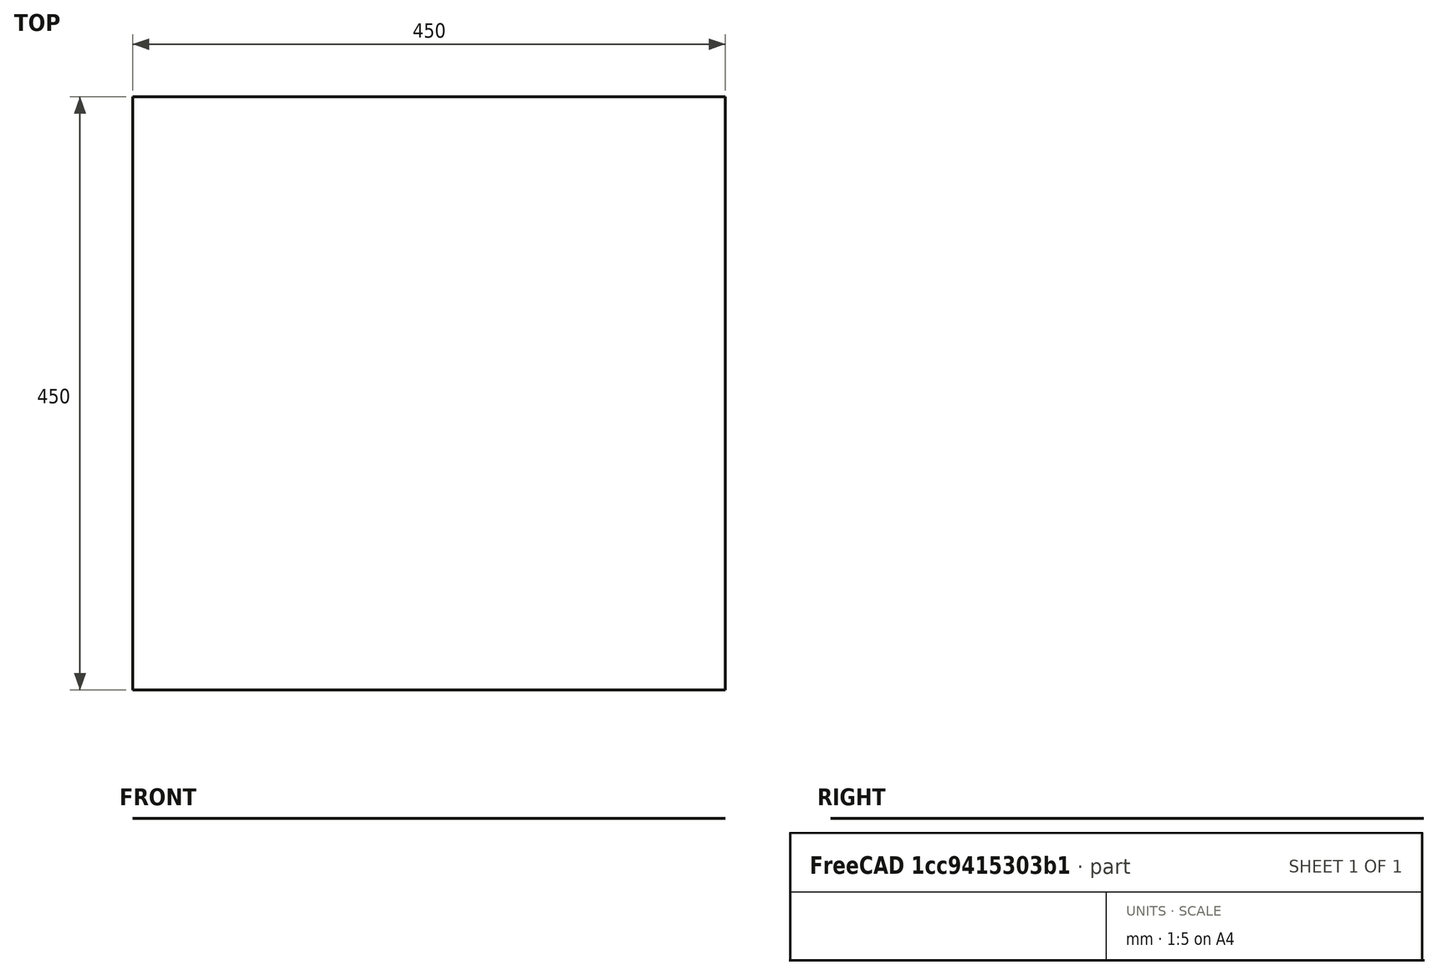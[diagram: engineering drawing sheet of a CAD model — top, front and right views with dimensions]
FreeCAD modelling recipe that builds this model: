
FCSTD DOCUMENT  (FreeCAD 0.19R18044 (Git))
Label: lift-upper-stage
License: Public Domain
LicenseURL: http://en.wikipedia.org/wiki/Public_domain
objects: App::FeaturePython×40, Part::FeaturePython×29, App::Link×6, App::LinkElement×4
note: 28 computed .brp shape members not serialized (recipe doc carries the construction recipe); baked Part::Feature solids carry a one-line shape summary decoded from their .brp
EXTERNAL_REF file=../parts/lift/upper-stage-actuator-rod.FCStd obj=Assembly
EXTERNAL_REF file=../parts/lift/upper-stage-beam.FCStd obj=Assembly
EXTERNAL_REF file=../parts/lift/upper-stage-beam.FCStd obj=Assembly001
EXTERNAL_REF file=../parts/lift/upper-stage-rod.FCStd obj=Assembly
EXTERNAL_REF file=../parts/common/linear-actuator-400.FCStd obj=Assembly004
EXTERNAL_REF file=../parts/common/rail-450.FCStd obj=Assembly002

FEATURE [App::Link] Link  label="upper-stage-actuator-rod"
  LinkPlacement = pos=(9.94618e-10,3.77807,437.103) rot=(-1,0,0;4.45001rad)
  LinkedObject = -> <external ../parts/lift/upper-stage-actuator-rod.FCStd>#Assembly
  Placement = pos=(9.94618e-10,3.77807,437.103) rot=(-1,0,0;4.45001rad)
FEATURE [App::Link] Link001  label="upper-stage-beam-left"
  LinkPlacement = pos=(-128,6.52807,7.10273) rot=(0,0,1;0rad)
  LinkedObject = -> <external ../parts/lift/upper-stage-beam.FCStd>#Assembly
  Placement = pos=(-128,6.52807,7.10273) rot=(0,0,1;0rad)
FEATURE [App::Link] Link002  label="upper-stage-beam-right"
  LinkPlacement = pos=(-118,6.52807,7.10273) rot=(0,0,1;0rad)
  LinkedObject = -> <external ../parts/lift/upper-stage-beam.FCStd>#Assembly001
  Placement = pos=(-118,6.52807,7.10273) rot=(0,0,1;0rad)
FEATURE [App::Link] Link004  label="actuator_a"
  LinkPlacement = pos=(9.25419e-08,3.77807,-78.8973) rot=(0,0,1;0rad)
  LinkedObject = -> <external ../parts/common/linear-actuator-400.FCStd>#Assembly004
  Placement = pos=(9.25419e-08,3.77807,-78.8973) rot=(0,0,1;0rad)
FEATURE [App::LinkElement] Link003_i0  label="top"
  LinkPlacement = pos=(3.02068e-10,-20.4719,357.103) rot=(0,0,1;0rad)
  LinkedObject = -> <external ../parts/lift/upper-stage-rod.FCStd>#Assembly
  Placement = pos=(3.02068e-10,-20.4719,357.103) rot=(0,0,1;0rad)
FEATURE [App::LinkElement] Link003_i1  label="bottom"
  LinkPlacement = pos=(7.62902e-11,-20.4719,227.103) rot=(0,0,1;0rad)
  LinkedObject = -> <external ../parts/lift/upper-stage-rod.FCStd>#Assembly
  Placement = pos=(7.62902e-11,-20.4719,227.103) rot=(0,0,1;0rad)
FEATURE [App::Link] Link003  label="upper-stage-rod"
  ElementCount = 2
  ElementList = -> [Link003_i0,Link003_i1]
  LinkedObject = -> <external ../parts/lift/upper-stage-rod.FCStd>#Assembly
FEATURE [App::LinkElement] Link005_i0  label="rail left"
  LinkPlacement = pos=(-93.3,31.0281,457.103) rot=(0.57735,-0.57735,-0.57735;2.0944rad)
  LinkedObject = -> <external ../parts/common/rail-450.FCStd>#Assembly002
  Placement = pos=(-93.3,31.0281,457.103) rot=(0.57735,-0.57735,-0.57735;2.0944rad)
FEATURE [App::LinkElement] Link005_i1  label="rail right"
  LinkPlacement = pos=(93.3,31.0281,457.103) rot=(0.57735,0.57735,0.57735;2.0944rad)
  LinkedObject = -> <external ../parts/common/rail-450.FCStd>#Assembly002
  Placement = pos=(93.3,31.0281,457.103) rot=(0.57735,0.57735,0.57735;2.0944rad)
FEATURE [App::Link] Link005  label="rail top"
  ElementCount = 2
  ElementList = -> [Link005_i0,Link005_i1]
  LinkedObject = -> <external ../parts/common/rail-450.FCStd>#Assembly002
FEATURE [Part::FeaturePython] Parts  # WARN: FeaturePython — macro-defined, semantics opaque (R4)
  Group = -> [Link,Link001,Link002,Link003,Link004,Origin,Link005]
  GroupMode = 0
FEATURE [Part::FeaturePython] Assembly  label="lift-upper-stage"  # WARN: FeaturePython — macro-defined, semantics opaque (R4)
  AutoRelax = true
  BuildShape = 0
  Freeze = false
  Group = -> [Constraints,Elements,Parts]
  GroupMode = 1
  SolverType = 1
  Verbose = false
  _SolverType = 1
  _Version = 1
FEATURE [App::FeaturePython] Constraints  # WARN: FeaturePython — macro-defined, semantics opaque (R4)
  Group = -> [Constraint,Constraint001,Constraint002,Constraint003,Constraint004,Constraint005,Constraint006,Constraint007,Constraint008,Constraint009,Constraint010,Constraint011,Constraint012]
  GroupMode = 1
  _Version = 1
FEATURE [App::FeaturePython] Elements  # WARN: FeaturePython — macro-defined, semantics opaque (R4)
  Group = -> [_Element,_Element001,_Element002,_Element003,_Element004,_Element005,_Element006,_Element007,_Element008,_Element009,_Element010,_Element011,_Element012,_Element013,_Element015,_Element016,_Element017,_Element018,_Element019,_Element020,_Element021,_Element022,_Element023,_Element024,_Element025,Element,Element001]
  GroupMode = 1
FEATURE [App::FeaturePython] Constraint  label="Locked"  # WARN: FeaturePython — macro-defined, semantics opaque (R4)
  ConstraintType = 0
  Disabled = false
  Group = -> [ElementLink]
  GroupMode = 1
  _ConstraintType = 0
  _Parent = -> Constraints
FEATURE [App::FeaturePython] ElementLink  label="_Element"  # link proxy (typed FeaturePython)
  LinkTransform = true
  LinkedObject = -> _Element
  _Parent = -> Constraint
FEATURE [Part::FeaturePython] _Element  # link proxy (typed FeaturePython)
  Detach = false
  LinkTransform = true
  LinkedObject = -> Link [1.$Element003.]
  _Parent = -> Elements
FEATURE [Part::FeaturePython] _Element001  # link proxy (typed FeaturePython)
  Detach = false
  LinkTransform = true
  LinkedObject = -> Link [1.$left.]
  _Parent = -> Elements
FEATURE [Part::FeaturePython] _Element002  # link proxy (typed FeaturePython)
  Detach = false
  LinkTransform = true
  LinkedObject = -> Link001 [1.$actuator_rod_hole.]
  _Parent = -> Elements
FEATURE [App::FeaturePython] Constraint001  label="PlaneCoincident"  # WARN: FeaturePython — macro-defined, semantics opaque (R4)
  Angle = 0
  AnglePitch = 0
  AngleRoll = 0
  Cascade = false
  ConstraintType = 2
  Disabled = false
  Group = -> [ElementLink001,ElementLink002]
  GroupMode = 1
  LockAngle = false
  Multiply = false
  Offset = -44
  OffsetX = 0
  OffsetY = 0
  _ConstraintType = 35
  _Parent = -> Constraints
FEATURE [App::FeaturePython] ElementLink001  label="_Element001"  # link proxy (typed FeaturePython)
  LinkTransform = true
  LinkedObject = -> _Element001
  _Parent = -> Constraint001
FEATURE [App::FeaturePython] ElementLink002  label="_Element002"  # link proxy (typed FeaturePython)
  LinkTransform = true
  LinkedObject = -> _Element002
  _Parent = -> Constraint001
FEATURE [App::FeaturePython] Constraint002  label="PlaneCoincident001"  # WARN: FeaturePython — macro-defined, semantics opaque (R4)
  Angle = 0
  AnglePitch = 0
  AngleRoll = 0
  Cascade = false
  ConstraintType = 2
  Disabled = false
  Group = -> [ElementLink003,ElementLink004]
  GroupMode = 1
  LockAngle = false
  Multiply = false
  Offset = -44
  OffsetX = 0
  OffsetY = 0
  _ConstraintType = 35
  _Parent = -> Constraints
FEATURE [App::FeaturePython] ElementLink003  label="_Element003"  # link proxy (typed FeaturePython)
  LinkTransform = true
  LinkedObject = -> _Element003
  _Parent = -> Constraint002
FEATURE [Part::FeaturePython] _Element003  # link proxy (typed FeaturePython)
  Detach = false
  LinkTransform = true
  LinkedObject = -> Link002 [1.$actuator_rod_hole.]
  _Parent = -> Elements
FEATURE [App::FeaturePython] ElementLink004  label="_Element004"  # link proxy (typed FeaturePython)
  LinkTransform = true
  LinkedObject = -> _Element004
  _Parent = -> Constraint002
FEATURE [Part::FeaturePython] _Element004  # link proxy (typed FeaturePython)
  Detach = false
  LinkTransform = true
  LinkedObject = -> Link [1.$right.]
  _Parent = -> Elements
FEATURE [App::FeaturePython] Constraint003  label="AxialAlignment"  # WARN: FeaturePython — macro-defined, semantics opaque (R4)
  Angle = 0
  AnglePitch = 0
  AngleRoll = 0
  ConstraintType = 4
  Disabled = false
  Group = -> [ElementLink005,ElementLink006]
  GroupMode = 1
  LockAngle = false
  Multiply = false
  _ConstraintType = 36
  _Parent = -> Constraints
FEATURE [App::FeaturePython] ElementLink005  label="_Element005"  # link proxy (typed FeaturePython)
  LinkTransform = true
  LinkedObject = -> _Element005
  _Parent = -> Constraint003
FEATURE [Part::FeaturePython] _Element005  # link proxy (typed FeaturePython)
  Detach = false
  LinkTransform = true
  LinkedObject = -> Link [1.$middle.]
  _Parent = -> Elements
FEATURE [App::FeaturePython] ElementLink006  label="_Element006"  # link proxy (typed FeaturePython)
  LinkTransform = true
  LinkedObject = -> _Element006
  _Parent = -> Constraint003
FEATURE [Part::FeaturePython] _Element006  # link proxy (typed FeaturePython)
  Detach = false
  LinkTransform = true
  LinkedObject = -> Link004 [1.$mount_top.]
  _Parent = -> Elements
FEATURE [App::FeaturePython] Constraint004  label="PlaneCoincident002"  # WARN: FeaturePython — macro-defined, semantics opaque (R4)
  Angle = 0
  AnglePitch = 0
  AngleRoll = 0
  Cascade = false
  ConstraintType = 2
  Disabled = false
  Group = -> [ElementLink007,ElementLink008]
  GroupMode = 1
  LockAngle = false
  Multiply = false
  Offset = -119
  OffsetX = 0
  OffsetY = 0
  _ConstraintType = 35
  _Parent = -> Constraints
FEATURE [App::FeaturePython] ElementLink007  label="_Element007"  # link proxy (typed FeaturePython)
  LinkTransform = true
  LinkedObject = -> _Element007
  _Parent = -> Constraint004
FEATURE [Part::FeaturePython] _Element007  # link proxy (typed FeaturePython)
  Detach = false
  LinkTransform = true
  LinkedObject = -> Link003 [Link003_i0.1.$left.]
  _Parent = -> Elements
FEATURE [App::FeaturePython] ElementLink008  label="_Element008"  # link proxy (typed FeaturePython)
  LinkTransform = true
  LinkedObject = -> _Element008
  _Parent = -> Constraint004
FEATURE [Part::FeaturePython] _Element008  # link proxy (typed FeaturePython)
  Detach = false
  LinkTransform = true
  LinkedObject = -> Link001 [1.$tv_rod_hole_top.]
  _Parent = -> Elements
FEATURE [App::FeaturePython] Constraint005  label="PlaneCoincident003"  # WARN: FeaturePython — macro-defined, semantics opaque (R4)
  Angle = 0
  AnglePitch = 0
  AngleRoll = 0
  Cascade = false
  ConstraintType = 2
  Disabled = false
  Group = -> [ElementLink009,ElementLink010]
  GroupMode = 1
  LockAngle = false
  Multiply = false
  Offset = 119
  OffsetX = 0
  OffsetY = 0
  _ConstraintType = 35
  _Parent = -> Constraints
FEATURE [App::FeaturePython] ElementLink009  label="_Element009"  # link proxy (typed FeaturePython)
  LinkTransform = true
  LinkedObject = -> _Element009
  _Parent = -> Constraint005
FEATURE [Part::FeaturePython] _Element009  # link proxy (typed FeaturePython)
  Detach = false
  LinkTransform = true
  LinkedObject = -> Link001 [1.$tv_rod_hole_bottom.]
  _Parent = -> Elements
FEATURE [App::FeaturePython] ElementLink010  label="_Element010"  # link proxy (typed FeaturePython)
  LinkTransform = true
  LinkedObject = -> _Element010
  _Parent = -> Constraint005
FEATURE [Part::FeaturePython] _Element010  # link proxy (typed FeaturePython)
  Detach = false
  LinkTransform = true
  LinkedObject = -> Link003 [Link003_i1.1.$left.]
  _Parent = -> Elements
FEATURE [Part::FeaturePython] _Element011  # link proxy (typed FeaturePython)
  Detach = false
  LinkTransform = true
  LinkedObject = -> Link002 [1.$tv_rod_hole_top.]
  _Parent = -> Elements
FEATURE [Part::FeaturePython] _Element012  # link proxy (typed FeaturePython)
  Detach = false
  LinkTransform = true
  LinkedObject = -> Link003 [Link003_i0.1.$right.]
  _Parent = -> Elements
FEATURE [App::FeaturePython] Constraint006  label="AxialAlignment001"  # WARN: FeaturePython — macro-defined, semantics opaque (R4)
  Angle = 0
  AnglePitch = 0
  AngleRoll = 0
  ConstraintType = 4
  Disabled = false
  Group = -> [ElementLink011,ElementLink012]
  GroupMode = 1
  LockAngle = false
  Multiply = false
  _ConstraintType = 36
  _Parent = -> Constraints
FEATURE [App::FeaturePython] ElementLink011  label="_Element011"  # link proxy (typed FeaturePython)
  LinkTransform = true
  LinkedObject = -> _Element011
  _Parent = -> Constraint006
FEATURE [App::FeaturePython] ElementLink012  label="_Element012"  # link proxy (typed FeaturePython)
  LinkTransform = true
  LinkedObject = -> _Element012
  _Parent = -> Constraint006
FEATURE [Part::FeaturePython] _Element013  # link proxy (typed FeaturePython)
  Detach = false
  LinkTransform = true
  LinkedObject = -> Link001 [1.$base_edge.]
  _Parent = -> Elements
FEATURE [Part::FeaturePython] _Element015  # link proxy (typed FeaturePython)
  Detach = false
  LinkTransform = true
  LinkedObject = -> Origin [Y_Axis.]
  _Parent = -> Elements
FEATURE [App::FeaturePython] Constraint007  label="MultiParallel"  # WARN: FeaturePython — macro-defined, semantics opaque (R4)
  Angle = 0
  AnglePitch = 0
  AngleRoll = 0
  ConstraintType = 6
  Disabled = false
  Group = -> [ElementLink013,ElementLink014]
  GroupMode = 1
  LockAngle = false
  _ConstraintType = 291
  _Parent = -> Constraints
FEATURE [App::FeaturePython] ElementLink013  label="_Element015"  # link proxy (typed FeaturePython)
  LinkTransform = true
  LinkedObject = -> _Element015
  _Parent = -> Constraint007
FEATURE [App::FeaturePython] ElementLink014  label="_Element013"  # link proxy (typed FeaturePython)
  LinkTransform = true
  LinkedObject = -> _Element013
  _Parent = -> Constraint007
FEATURE [Part::FeaturePython] _Element016  # link proxy (typed FeaturePython)
  Detach = false
  LinkTransform = true
  LinkedObject = -> Link001 [1.$rail_hole_top.]
  _Parent = -> Elements
FEATURE [Part::FeaturePython] _Element017  # link proxy (typed FeaturePython)
  Detach = false
  LinkTransform = true
  LinkedObject = -> Link005 [Link005_i0.1.$mount_top.]
  _Parent = -> Elements
FEATURE [Part::FeaturePython] _Element018  # link proxy (typed FeaturePython)
  Detach = false
  LinkTransform = true
  LinkedObject = -> Link001 [1.$rail-hole-middle.]
  _Parent = -> Elements
FEATURE [Part::FeaturePython] _Element019  # link proxy (typed FeaturePython)
  Detach = false
  LinkTransform = true
  LinkedObject = -> Link005 [Link005_i0.1.$mount_middle.]
  _Parent = -> Elements
FEATURE [App::FeaturePython] Constraint008  label="PlaneCoincident004"  # WARN: FeaturePython — macro-defined, semantics opaque (R4)
  Angle = 0
  AnglePitch = 0
  AngleRoll = 0
  Cascade = false
  ConstraintType = 2
  Disabled = false
  Group = -> [ElementLink015,ElementLink016]
  GroupMode = 1
  LockAngle = false
  Multiply = false
  OffsetX = 0
  OffsetY = 0
  _ConstraintType = 35
  _Parent = -> Constraints
FEATURE [App::FeaturePython] ElementLink015  label="_Element016"  # link proxy (typed FeaturePython)
  LinkTransform = true
  LinkedObject = -> _Element016
  _Parent = -> Constraint008
FEATURE [App::FeaturePython] ElementLink016  label="_Element017"  # link proxy (typed FeaturePython)
  LinkTransform = true
  LinkedObject = -> _Element017
  _Parent = -> Constraint008
FEATURE [App::FeaturePython] Constraint009  label="PlaneCoincident005"  # WARN: FeaturePython — macro-defined, semantics opaque (R4)
  Angle = 0
  AnglePitch = 0
  AngleRoll = 0
  Cascade = false
  ConstraintType = 2
  Disabled = false
  Group = -> [ElementLink017,ElementLink018]
  GroupMode = 1
  LockAngle = false
  Multiply = false
  OffsetX = 0
  OffsetY = 0
  _ConstraintType = 35
  _Parent = -> Constraints
FEATURE [App::FeaturePython] ElementLink017  label="_Element019"  # link proxy (typed FeaturePython)
  LinkTransform = true
  LinkedObject = -> _Element019
  _Parent = -> Constraint009
FEATURE [App::FeaturePython] ElementLink018  label="_Element018"  # link proxy (typed FeaturePython)
  LinkTransform = true
  LinkedObject = -> _Element018
  _Parent = -> Constraint009
FEATURE [App::FeaturePython] Constraint010  label="PlaneCoincident006"  # WARN: FeaturePython — macro-defined, semantics opaque (R4)
  Angle = 0
  AnglePitch = 0
  AngleRoll = 0
  Cascade = false
  ConstraintType = 2
  Disabled = false
  Group = -> [ElementLink019,ElementLink020]
  GroupMode = 1
  LockAngle = false
  Multiply = false
  OffsetX = 0
  OffsetY = 0
  _ConstraintType = 35
  _Parent = -> Constraints
FEATURE [App::FeaturePython] ElementLink019  label="_Element020"  # link proxy (typed FeaturePython)
  LinkTransform = true
  LinkedObject = -> _Element020
  _Parent = -> Constraint010
FEATURE [Part::FeaturePython] _Element020  # link proxy (typed FeaturePython)
  Detach = false
  LinkTransform = true
  LinkedObject = -> Link005 [Link005_i1.1.$mount_top.]
  _Parent = -> Elements
FEATURE [App::FeaturePython] ElementLink020  label="_Element021"  # link proxy (typed FeaturePython)
  LinkTransform = true
  LinkedObject = -> _Element021
  _Parent = -> Constraint010
FEATURE [Part::FeaturePython] _Element021  # link proxy (typed FeaturePython)
  Detach = false
  LinkTransform = true
  LinkedObject = -> Link002 [1.$rail_hole_top.]
  _Parent = -> Elements
FEATURE [App::FeaturePython] Constraint011  label="PlaneCoincident007"  # WARN: FeaturePython — macro-defined, semantics opaque (R4)
  Angle = 0
  AnglePitch = 0
  AngleRoll = 0
  Cascade = false
  ConstraintType = 2
  Disabled = false
  Group = -> [ElementLink021,ElementLink022]
  GroupMode = 1
  LockAngle = false
  Multiply = false
  OffsetX = 0
  OffsetY = 0
  _ConstraintType = 35
  _Parent = -> Constraints
FEATURE [App::FeaturePython] ElementLink021  label="_Element022"  # link proxy (typed FeaturePython)
  LinkTransform = true
  LinkedObject = -> _Element022
  _Parent = -> Constraint011
FEATURE [Part::FeaturePython] _Element022  # link proxy (typed FeaturePython)
  Detach = false
  LinkTransform = true
  LinkedObject = -> Link002 [1.$rail_hole_middle.]
  _Parent = -> Elements
FEATURE [App::FeaturePython] ElementLink022  label="_Element023"  # link proxy (typed FeaturePython)
  LinkTransform = true
  LinkedObject = -> _Element023
  _Parent = -> Constraint011
FEATURE [Part::FeaturePython] _Element023  # link proxy (typed FeaturePython)
  Detach = false
  LinkTransform = true
  LinkedObject = -> Link005 [Link005_i1.1.$mount_middle.]
  _Parent = -> Elements
FEATURE [App::FeaturePython] Constraint012  label="MultiParallel001"  # WARN: FeaturePython — macro-defined, semantics opaque (R4)
  Angle = 0
  AnglePitch = 0
  AngleRoll = 0
  ConstraintType = 6
  Disabled = false
  Group = -> [ElementLink023,ElementLink024]
  GroupMode = 1
  LockAngle = false
  _ConstraintType = 291
  _Parent = -> Constraints
FEATURE [App::FeaturePython] ElementLink023  label="_Element024"  # link proxy (typed FeaturePython)
  LinkTransform = true
  LinkedObject = -> _Element024
  _Parent = -> Constraint012
FEATURE [Part::FeaturePython] _Element024  # link proxy (typed FeaturePython)
  Detach = false
  LinkTransform = true
  LinkedObject = -> Origin [XY_Plane.]
  _Parent = -> Elements
FEATURE [App::FeaturePython] ElementLink024  label="_Element025"  # link proxy (typed FeaturePython)
  LinkTransform = true
  LinkedObject = -> _Element025
  _Parent = -> Constraint012
FEATURE [Part::FeaturePython] _Element025  # link proxy (typed FeaturePython)
  Detach = false
  LinkTransform = true
  LinkedObject = -> Link004 [1.$_Element.]
  _Parent = -> Elements
FEATURE [Part::FeaturePython] Element  # link proxy (typed FeaturePython)
  Detach = false
  LinkTransform = true
  LinkedObject = -> Link005 [Link005_i0.1.$slide_axis.]
  _Parent = -> Elements
FEATURE [Part::FeaturePython] Element001  # link proxy (typed FeaturePython)
  Detach = false
  LinkTransform = true
  LinkedObject = -> Link005 [Link005_i1.1.$slide_axis.]
  _Parent = -> Elements

RESOLVED EXTERNAL PARTS (link-assembly join: the EXTERNAL_REF files above that resolve inside this repo's crawl, each included once):
---- part ../parts/common/linear-actuator-400.FCStd = doc fcstd_0eb58a5116f6 ----
FCSTD DOCUMENT  (FreeCAD 0.19R18044 (Git))
Label: linear-actuator-400
License: Public Domain
LicenseURL: http://en.wikipedia.org/wiki/Public_domain
objects: Part::FeaturePython×21, App::FeaturePython×19, Sketcher::SketchObject×15, PartDesign::Pad×8, PartDesign::Pocket×6, PartDesign::Body×4, PartDesign::Hole×1
note: 66 computed .brp shape members not serialized (recipe doc carries the construction recipe); baked Part::Feature solids carry a one-line shape summary decoded from their .brp

FEATURE [Sketcher::SketchObject] Sketch
  MapMode = 5
  Support = -> [XY_Plane]
  sketch-geometry (6):
    g0: LineSegment StartX=-10 StartY=20 StartZ=0 EndX=-20 EndY=11.609 EndZ=0
    g1: LineSegment StartX=-20 StartY=11.609 StartZ=0 EndX=-20 EndY=-35 EndZ=0
    g2: LineSegment StartX=20 StartY=-35 StartZ=0 EndX=20 EndY=11.609 EndZ=0
    g3: LineSegment StartX=20 StartY=11.609 StartZ=0 EndX=10 EndY=20 EndZ=0
    g4: LineSegment StartX=10 StartY=20 StartZ=0 EndX=-10 EndY=20 EndZ=0
    g5: ArcOfCircle CenterX=-4e-16 CenterY=-35 CenterZ=0 NormalX=0 NormalY=0 NormalZ=1 AngleXU=0 Radius=20 StartAngle=3.14159 EndAngle=6.28319
  constraints (18):
    c: Coincident(g0,g1)
    c: Vertical(g1)
    c: Vertical(g2)
    c: Coincident(g2,g3)
    c: Coincident(g3,g4)
    c: Coincident(g4,g0)
    c: Horizontal(g4)
    c: Symmetric(g0,g2,g-2)
    c: Equal(g0,g3)
    c: Coincident(g5,g1)
    c: Coincident(g5,g2)
    c: Radius(g5) = 20
    c: Horizontal(g5,g2)
    c: Horizontal(g2,g1)
    c: DistanceY(g2,g3) = 55
    c: DistanceY(g-1,g3) = 20
    c: Distance(g4) = 20
    c: Angle(g1,g0) = 2.26893
FEATURE [PartDesign::Pad] Pad  label="base"
  ClaimChildren = false
  Length = 22
  Length2 = 100
  Profile = -> Sketch
  Type = 0
FEATURE [Sketcher::SketchObject] Sketch001
  MapMode = 5
  Placement = pos=(0,0,0) rot=(1,0,0;3.14159rad)
  Support = -> [Pad]
  sketch-geometry (9):
    g0: LineSegment StartX=-4.3589 StartY=9 StartZ=0 EndX=4.3589 EndY=9 EndZ=0
    g1: LineSegment StartX=9 StartY=4.3589 StartZ=0 EndX=9 EndY=-4.3589 EndZ=0
    g2: LineSegment StartX=4.3589 StartY=-9 StartZ=0 EndX=-4.3589 EndY=-9 EndZ=0
    g3: LineSegment StartX=-9 StartY=-4.3589 StartZ=0 EndX=-9 EndY=4.3589 EndZ=0
    g4: Circle [constr] CenterX=0 CenterY=0 CenterZ=0 NormalX=0 NormalY=0 NormalZ=1 AngleXU=0 Radius=10
    g5: ArcOfCircle CenterX=0 CenterY=0 CenterZ=0 NormalX=0 NormalY=0 NormalZ=1 AngleXU=0 Radius=10 StartAngle=2.02182 EndAngle=2.69057
    g6: ArcOfCircle CenterX=0 CenterY=0 CenterZ=0 NormalX=0 NormalY=0 NormalZ=1 AngleXU=0 Radius=10 StartAngle=0.451027 EndAngle=1.11977
    g7: ArcOfCircle CenterX=0 CenterY=0 CenterZ=0 NormalX=0 NormalY=0 NormalZ=1 AngleXU=0 Radius=10 StartAngle=5.16342 EndAngle=5.83216
    g8: ArcOfCircle CenterX=0 CenterY=0 CenterZ=0 NormalX=0 NormalY=0 NormalZ=1 AngleXU=0 Radius=10 StartAngle=3.59262 EndAngle=4.26136
  constraints (25):
    c: Horizontal(g0)
    c: Vertical(g1)
    c: Vertical(g3)
    c: Coincident(g4,g-1)
    c: Equal(g0,g1)
    c: Radius(g4) = 10
    c: Coincident(g5,g3)
    c: Coincident(g0,g5)
    c: Coincident(g-1,g5)
    c: Radius(g5) = 10
    c: Coincident(g2,g8)
    c: Coincident(g2,g7)
    c: Coincident(g1,g7)
    c: Coincident(g1,g6)
    c: Coincident(g0,g6)
    c: Coincident(g8,g5)
    c: Coincident(g8,g3)
    c: Coincident(g7,g5)
    c: Coincident(g6,g5)
    c: Radius(g6) = 10
    c: Radius(g7) = 10
    c: DistanceY(g2,g0) = 18
    c: DistanceX(g3,g1) = 18
    c: Symmetric(g2,g2,g-2)
    c: Vertical(g0,g2)
FEATURE [PartDesign::Pad] Pad001  label="foot"
  BaseFeature = -> Pad
  ClaimChildren = false
  Length = 19
  Length2 = 100
  Profile = -> Sketch001
  Type = 0
FEATURE [Sketcher::SketchObject] Sketch002
  MapMode = 5
  Placement = pos=(-9,0,0) rot=(0.57735,-0.57735,-0.57735;2.0944rad)
  Support = -> [Pad001]
  sketch-geometry (1):
    g0: Circle CenterX=0 CenterY=-11 CenterZ=0 NormalX=0 NormalY=0 NormalZ=1 AngleXU=0 Radius=3.25
  constraints (3):
    c: PointOnObject(g0,g-2)
    c: Diameter(g0) = 6.5
    c: DistanceY(g0,g-1) = 11
FEATURE [PartDesign::Hole] Hole
  BaseFeature = -> Pad001
  ClaimChildren = false
  Depth = 25
  DepthType = 1
  Diameter = 6
  DrillPoint = 1
  DrillPointAngle = 118
  HoleCutCountersinkAngle = 90
  HoleCutDepth = 0
  HoleCutDiameter = 0
  HoleCutType = 0
  ModelActualThread = false
  Profile = -> Sketch002
  Tapered = false
  TaperedAngle = 90
  ThreadAngle = 0
  ThreadClass = 0
  ThreadCutOffInner = 0
  ThreadCutOffOuter = 0
  ThreadDirection = 0
  ThreadFit = 0
  ThreadPitch = 0
  ThreadSize = 0
  ThreadType = 0
  Threaded = false
FEATURE [Sketcher::SketchObject] Sketch003
  ExternalGeometry = -> [Hole]
  MapMode = 5
  Placement = pos=(0,0,22) rot=(0,0,1;0rad)
  Support = -> [Hole]
  sketch-geometry (4):
    g0: LineSegment StartX=-15 StartY=1.8e-15 StartZ=0 EndX=-10 EndY=20 EndZ=0
    g1: LineSegment StartX=-10 StartY=20 StartZ=0 EndX=10 EndY=20 EndZ=0
    g2: LineSegment StartX=10 StartY=20 StartZ=0 EndX=15 EndY=-3.6e-15 EndZ=0
    g3: ArcOfCircle CenterX=0 CenterY=0 CenterZ=0 NormalX=0 NormalY=0 NormalZ=1 AngleXU=0 Radius=15 StartAngle=3.14159 EndAngle=6.28319
  constraints (12):
    c: Coincident(g0,g1)
    c: Horizontal(g1)
    c: Coincident(g1,g2)
    c: Coincident(g3,g-1)
    c: Coincident(g3,g0)
    c: Coincident(g3,g2)
    c: Diameter(g3) = 30
    c: PointOnObject(g0,g-3)
    c: DistanceX(g1,g1) = 20
    c: Equal(g2,g0)
    c: Symmetric(g2,g0,g-2)
    c: PointOnObject(g2,g-1)
FEATURE [PartDesign::Pad] Pad002
  BaseFeature = -> Hole
  ClaimChildren = false
  Length = 500
  Length2 = 100
  Profile = -> Sketch003
  Type = 0
FEATURE [Sketcher::SketchObject] Sketch004
  MapMode = 5
  Placement = pos=(0,0,522) rot=(0,0,1;0rad)
  Support = -> [Pad002]
  sketch-geometry (1):
    g0: Circle CenterX=0 CenterY=0 CenterZ=0 NormalX=0 NormalY=0 NormalZ=1 AngleXU=0 Radius=10
  constraints (2):
    c: Coincident(g0,g-1)
    c: Diameter(g0) = 20
FEATURE [PartDesign::Pocket] Pocket
  BaseFeature = -> Pad002
  ClaimChildren = false
  Length = 500
  Length2 = 100
  Profile = -> Sketch004
  Type = 0
FEATURE [Sketcher::SketchObject] Sketch005
  MapMode = 5
  Support = -> [XY_Plane001]
  sketch-geometry (1):
    g0: Circle CenterX=0 CenterY=0 CenterZ=0 NormalX=0 NormalY=0 NormalZ=1 AngleXU=0 Radius=10
  constraints (2):
    c: Coincident(g0,g-1)
    c: Diameter(g0) = 20
FEATURE [PartDesign::Pad] Pad003
  ClaimChildren = false
  Length = 523
  Length2 = 100
  Profile = -> Sketch005
  Type = 0
FEATURE [Sketcher::SketchObject] Sketch006
  ExternalGeometry = -> [Pad003]
  MapMode = 5
  Placement = pos=(0,0,0) rot=(0.57735,0.57735,0.57735;2.0944rad)
  Support = -> [YZ_Plane001]
  sketch-geometry (1):
    g0: Circle CenterX=-1.11e-13 CenterY=514 CenterZ=0 NormalX=0 NormalY=0 NormalZ=1 AngleXU=0 Radius=3.25
  constraints (3):
    c: DistanceY(g0,g-3) = 9
    c: PointOnObject(g0,g-3)
    c: Diameter(g0) = 6.5
FEATURE [PartDesign::Pocket] Pocket001
  BaseFeature = -> Pad003
  ClaimChildren = false
  Length = 5
  Length2 = 100
  Midplane = true
  Profile = -> Sketch006
  Type = 1
FEATURE [PartDesign::Body] Body001  label="piston"
  Group = -> [Sketch005,Pad003,Sketch006,Pocket001]
  Origin = -> Origin001
  Placement = pos=(0,0,22) rot=(0,0,1;0rad)
  SingleSolid = true
  Tip = -> Pocket001
FEATURE [Sketcher::SketchObject] Sketch007
  MapMode = 5
  Placement = pos=(0,0,22) rot=(0,0,1;0rad)
  Support = -> [Pocket]
  sketch-geometry (1):
    g0: Circle CenterX=0 CenterY=-35 CenterZ=0 NormalX=0 NormalY=0 NormalZ=1 AngleXU=0 Radius=19
  constraints (3):
    c: PointOnObject(g0,g-2)
    c: Diameter(g0) = 38
    c: DistanceY(g0,g-1) = 35
FEATURE [PartDesign::Pad] Pad004
  BaseFeature = -> Pocket
  ClaimChildren = false
  Length = 77
  Length2 = 100
  Profile = -> Sketch007
  Type = 0
FEATURE [Sketcher::SketchObject] Sketch008
  MapMode = 5
  Placement = pos=(0,0,99) rot=(0,0,1;0rad)
  Support = -> [Pad004]
  sketch-geometry (1):
    g0: Circle CenterX=0 CenterY=-35 CenterZ=0 NormalX=0 NormalY=0 NormalZ=1 AngleXU=0 Radius=6.25
  constraints (3):
    c: PointOnObject(g0,g-2)
    c: DistanceY(g0,g-1) = 35
    c: Diameter(g0) = 12.5
FEATURE [PartDesign::Pad] Pad005
  BaseFeature = -> Pad004
  ClaimChildren = false
  Length = 2
  Length2 = 100
  Profile = -> Sketch008
  Type = 0
FEATURE [PartDesign::Body] Body  label="actuator base"
  Group = -> [Sketch,Pad,Sketch001,Pad001,Sketch002,Hole,Sketch003,Pad002,Sketch004,Pocket,Sketch007,Pad004,Sketch008,Pad005]
  Origin = -> Origin
  SingleSolid = true
  Tip = -> Pad005
FEATURE [Sketcher::SketchObject] Sketch009
  MapMode = 5
  Placement = pos=(0,0,0) rot=(1,0,0;1.5708rad)
  Support = -> [XZ_Plane002]
  sketch-geometry (7):
    g0: LineSegment StartX=-8.5 StartY=1e-15 StartZ=0 EndX=-8.5 EndY=-36.5 EndZ=0
    g1: LineSegment StartX=-8.5 StartY=-36.5 StartZ=0 EndX=49.5 EndY=-36.5 EndZ=0
    g2: LineSegment StartX=49.5 StartY=-36.5 StartZ=0 EndX=49.5 EndY=-21.5 EndZ=0
    g3: LineSegment StartX=49.5 StartY=-21.5 StartZ=0 EndX=3.04099 EndY=7.9374 EndZ=0
    g4: ArcOfCircle CenterX=0 CenterY=0 CenterZ=0 NormalX=0 NormalY=0 NormalZ=1 AngleXU=0 Radius=8.5 StartAngle=1.20492 EndAngle=3.14159
    g5: Circle CenterX=0 CenterY=0 CenterZ=0 NormalX=0 NormalY=0 NormalZ=1 AngleXU=0 Radius=3
    g6: GeomPoint X=1.97567e-07 Y=8.5 Z=0
  constraints (19):
    c: Vertical(g0)
    c: Coincident(g0,g1)
    c: Horizontal(g1)
    c: Coincident(g1,g2)
    c: Vertical(g2)
    c: Coincident(g2,g3)
    c: Coincident(g4,g-1)
    c: Coincident(g4,g0)
    c: Coincident(g4,g3)
    c: Coincident(g5,g4)
    c: Distance(g1) = 58
    c: Distance(g0) = 36.5
    c: Distance(g2) = 15
    c: Diameter(g5) = 6
    c: DistanceX(g0,g4) = 8.5
    c: PointOnObject(g0,g-1)
    c: PointOnObject(g6,g4)
    c: DistanceY(g0,g6) = 45
    c: Distance(g3) = 55
FEATURE [PartDesign::Pad] Pad006
  ClaimChildren = false
  Length = 25.5
  Length2 = 100
  Midplane = true
  Placement = pos=(0,0,0) rot=(1,0,0;1.5708rad)
  Profile = -> Sketch009
  Type = 0
FEATURE [Sketcher::SketchObject] Sketch010
  ExternalGeometry = -> [Pad006]
  MapMode = 5
  Placement = pos=(-8.5,0,0) rot=(0.707107,0,-0.707107;3.14159rad)
  Support = -> [Pad006]
  sketch-geometry (4):
    g0: LineSegment StartX=-11.5 StartY=9.75 StartZ=0 EndX=33.5 EndY=9.75 EndZ=0
    g1: LineSegment StartX=33.5 StartY=9.75 StartZ=0 EndX=33.5 EndY=-9.75 EndZ=0
    g2: LineSegment StartX=33.5 StartY=-9.75 StartZ=0 EndX=-11.5 EndY=-9.75 EndZ=0
    g3: LineSegment StartX=-11.5 StartY=-9.75 StartZ=0 EndX=-11.5 EndY=9.75 EndZ=0
  constraints (11):
    c: Coincident(g0,g1)
    c: Coincident(g1,g2)
    c: Coincident(g2,g3)
    c: Coincident(g3,g0)
    c: Horizontal(g0)
    c: Horizontal(g2)
    c: Vertical(g3)
    c: Symmetric(g0,g1,g-1)
    c: DistanceX(g0,g-3) = 3
    c: DistanceY(g0,g-3) = 3
    c: Distance(g0) = 45
FEATURE [PartDesign::Pocket] Pocket002
  BaseFeature = -> Pad006
  ClaimChildren = false
  Length = 5
  Length2 = 100
  Placement = pos=(0,0,0) rot=(1,0,0;1.5708rad)
  Profile = -> Sketch010
  Type = 1
FEATURE [Sketcher::SketchObject] Sketch011
  ExternalGeometry = -> [Pocket002]
  MapMode = 5
  Placement = pos=(7.4e-15,0,-33.5) rot=(0,0,1;3.14159rad)
  Support = -> [Pocket002]
  sketch-geometry (5):
    g0: Circle CenterX=-37 CenterY=0 CenterZ=0 NormalX=0 NormalY=0 NormalZ=1 AngleXU=0 Radius=4
    g1: LineSegment StartX=-1.5 StartY=4.25 StartZ=0 EndX=8.5 EndY=4.25 EndZ=0
    g2: LineSegment StartX=-1.5 StartY=-4.25 StartZ=0 EndX=8.5 EndY=-4.25 EndZ=0
    g3: ArcOfCircle CenterX=-1.5 CenterY=4e-16 CenterZ=0 NormalX=0 NormalY=0 NormalZ=1 AngleXU=0 Radius=4.25 StartAngle=1.5708 EndAngle=4.71239
    g4: LineSegment StartX=8.5 StartY=4.25 StartZ=0 EndX=8.5 EndY=-4.25 EndZ=0
  constraints (15):
    c: PointOnObject(g0,g-1)
    c: PointOnObject(g1,g-3)
    c: Horizontal(g1)
    c: PointOnObject(g2,g-3)
    c: Horizontal(g2)
    c: Symmetric(g1,g2,g-1)
    c: Coincident(g3,g2)
    c: Coincident(g3,g1)
    c: DistanceX(g3,g-3) = 10
    c: Distance(g1) = 10
    c: Diameter(g3) = 8.5
    c: Diameter(g0) = 8
    c: DistanceX(g0,g-3) = 45.5
    c: Coincident(g4,g1)
    c: Coincident(g4,g2)
FEATURE [PartDesign::Pocket] Pocket003
  BaseFeature = -> Pocket002
  ClaimChildren = false
  Length = 5
  Length2 = 100
  Placement = pos=(0,0,0) rot=(1,0,0;1.5708rad)
  Profile = -> Sketch011
  Type = 1
FEATURE [PartDesign::Body] Body002  label="bracket bottom"
  Group = -> [Sketch009,Pad006,Sketch010,Pocket002,Sketch011,Pocket003]
  Origin = -> Origin002
  Placement = pos=(0,0,-11) rot=(0,0,1;4.71239rad)
  SingleSolid = true
  Tip = -> Pocket003
FEATURE [Sketcher::SketchObject] Sketch012
  MapMode = 5
  Placement = pos=(0,0,0) rot=(1,0,0;1.5708rad)
  Support = -> [XZ_Plane003]
  sketch-geometry (7):
    g0: LineSegment StartX=-8.5 StartY=1e-15 StartZ=0 EndX=-8.5 EndY=-36.5 EndZ=0
    g1: LineSegment StartX=-8.5 StartY=-36.5 StartZ=0 EndX=49.5 EndY=-36.5 EndZ=0
    g2: LineSegment StartX=49.5 StartY=-36.5 StartZ=0 EndX=49.5 EndY=-21.5 EndZ=0
    g3: LineSegment StartX=49.5 StartY=-21.5 StartZ=0 EndX=3.04099 EndY=7.9374 EndZ=0
    g4: ArcOfCircle CenterX=0 CenterY=0 CenterZ=0 NormalX=0 NormalY=0 NormalZ=1 AngleXU=0 Radius=8.5 StartAngle=1.20492 EndAngle=3.14159
    g5: Circle CenterX=0 CenterY=0 CenterZ=0 NormalX=0 NormalY=0 NormalZ=1 AngleXU=0 Radius=3
    g6: GeomPoint X=2.60784e-05 Y=8.5 Z=0
  constraints (19):
    c: Vertical(g0)
    c: Coincident(g0,g1)
    c: Horizontal(g1)
    c: Coincident(g1,g2)
    c: Vertical(g2)
    c: Coincident(g2,g3)
    c: Coincident(g4,g-1)
    c: Coincident(g4,g0)
    c: Coincident(g4,g3)
    c: Coincident(g5,g4)
    c: Distance(g1) = 58
    c: Distance(g0) = 36.5
    c: Distance(g2) = 15
    c: Diameter(g5) = 6
    c: DistanceX(g0,g4) = 8.5
    c: PointOnObject(g0,g-1)
    c: PointOnObject(g6,g4)
    c: DistanceY(g0,g6) = 45
    c: Distance(g3) = 55
FEATURE [PartDesign::Pad] Pad007
  ClaimChildren = false
  Length = 25.5
  Length2 = 100
  Midplane = true
  Placement = pos=(0,0,0) rot=(1,0,0;1.5708rad)
  Profile = -> Sketch012
  Type = 0
FEATURE [Sketcher::SketchObject] Sketch013
  ExternalGeometry = -> [Pad007]
  MapMode = 5
  Placement = pos=(-8.5,0,0) rot=(0.707107,0,-0.707107;3.14159rad)
  Support = -> [Pad007]
  sketch-geometry (4):
    g0: LineSegment StartX=-11.5 StartY=9.75 StartZ=0 EndX=33.5 EndY=9.75 EndZ=0
    g1: LineSegment StartX=33.5 StartY=9.75 StartZ=0 EndX=33.5 EndY=-9.75 EndZ=0
    g2: LineSegment StartX=33.5 StartY=-9.75 StartZ=0 EndX=-11.5 EndY=-9.75 EndZ=0
    g3: LineSegment StartX=-11.5 StartY=-9.75 StartZ=0 EndX=-11.5 EndY=9.75 EndZ=0
  constraints (11):
    c: Coincident(g0,g1)
    c: Coincident(g1,g2)
    c: Coincident(g2,g3)
    c: Coincident(g3,g0)
    c: Horizontal(g0)
    c: Horizontal(g2)
    c: Vertical(g3)
    c: Symmetric(g0,g1,g-1)
    c: DistanceX(g0,g-3) = 3
    c: DistanceY(g0,g-3) = 3
    c: Distance(g0) = 45
FEATURE [PartDesign::Pocket] Pocket004
  BaseFeature = -> Pad007
  ClaimChildren = false
  Length = 5
  Length2 = 100
  Placement = pos=(0,0,0) rot=(1,0,0;1.5708rad)
  Profile = -> Sketch013
  Type = 1
FEATURE [Sketcher::SketchObject] Sketch014
  ExternalGeometry = -> [Pocket004]
  MapMode = 5
  Placement = pos=(7.4e-15,0,-33.5) rot=(0,0,1;3.14159rad)
  Support = -> [Pocket004]
  sketch-geometry (5):
    g0: Circle CenterX=-37 CenterY=0 CenterZ=0 NormalX=0 NormalY=0 NormalZ=1 AngleXU=0 Radius=4
    g1: LineSegment StartX=-1.5 StartY=4.25 StartZ=0 EndX=8.5 EndY=4.25 EndZ=0
    g2: LineSegment StartX=-1.5 StartY=-4.25 StartZ=0 EndX=8.5 EndY=-4.25 EndZ=0
    g3: ArcOfCircle CenterX=-1.5 CenterY=4e-16 CenterZ=0 NormalX=0 NormalY=0 NormalZ=1 AngleXU=0 Radius=4.25 StartAngle=1.5708 EndAngle=4.71239
    g4: LineSegment StartX=8.5 StartY=4.25 StartZ=0 EndX=8.5 EndY=-4.25 EndZ=0
  constraints (15):
    c: PointOnObject(g0,g-1)
    c: PointOnObject(g1,g-3)
    c: Horizontal(g1)
    c: PointOnObject(g2,g-3)
    c: Horizontal(g2)
    c: Symmetric(g1,g2,g-1)
    c: Coincident(g3,g2)
    c: Coincident(g3,g1)
    c: DistanceX(g3,g-3) = 10
    c: Distance(g1) = 10
    c: Diameter(g3) = 8.5
    c: Diameter(g0) = 8
    c: DistanceX(g0,g-3) = 45.5
    c: Coincident(g4,g1)
    c: Coincident(g4,g2)
FEATURE [PartDesign::Pocket] Pocket005
  BaseFeature = -> Pocket004
  ClaimChildren = false
  Length = 5
  Length2 = 100
  Placement = pos=(0,0,0) rot=(1,0,0;1.5708rad)
  Profile = -> Sketch014
  Type = 1
FEATURE [PartDesign::Body] Body003  label="bracket top"
  Group = -> [Sketch012,Pad007,Sketch013,Pocket004,Sketch014,Pocket005]
  Origin = -> Origin003
  Placement = pos=(2e-15,0,536) rot=(-0.707107,0.707107,0;3.14159rad)
  SingleSolid = true
  Tip = -> Pocket005
FEATURE [App::FeaturePython] Constraints  # WARN: FeaturePython — macro-defined, semantics opaque (R4)
  GroupMode = 1
  _Version = 1
FEATURE [Part::FeaturePython] Parts  label="Parts_Bracket"  # WARN: FeaturePython — macro-defined, semantics opaque (R4)
  Group = -> [Body002]
  GroupMode = 0
FEATURE [App::FeaturePython] Constraints002  # WARN: FeaturePython — macro-defined, semantics opaque (R4)
  GroupMode = 1
  _Version = 1
FEATURE [Part::FeaturePython] Parts002  label="Parts_Piston"  # WARN: FeaturePython — macro-defined, semantics opaque (R4)
  Group = -> [Body001]
  GroupMode = 0
FEATURE [App::FeaturePython] Constraints003  # WARN: FeaturePython — macro-defined, semantics opaque (R4)
  GroupMode = 1
  _Version = 1
FEATURE [Part::FeaturePython] Parts003  label="Parts_Base"  # WARN: FeaturePython — macro-defined, semantics opaque (R4)
  Group = -> [Body]
  GroupMode = 0
FEATURE [Part::FeaturePython] Assembly  label="bracket_a"  # WARN: FeaturePython — macro-defined, semantics opaque (R4)
  AutoRelax = true
  BuildShape = 0
  Freeze = false
  Group = -> [Constraints,Elements,Parts]
  GroupMode = 1
  Placement = pos=(0,2.38419e-06,-20) rot=(0,0,1;0rad)
  SolverType = 1
  Verbose = false
  _SolverType = 1
  _Version = 1
FEATURE [App::FeaturePython] Elements  label="Elements_Bracket"  # WARN: FeaturePython — macro-defined, semantics opaque (R4)
  Group = -> [Element,Element001,Element003]
  GroupMode = 1
FEATURE [Part::FeaturePython] Assembly002  label="piston_a"  # WARN: FeaturePython — macro-defined, semantics opaque (R4)
  AutoRelax = true
  BuildShape = 0
  Freeze = false
  Group = -> [Constraints002,Elements002,Parts002]
  GroupMode = 1
  Placement = pos=(1.7e-15,2.38418e-06,-20) rot=(0,0,1;0rad)
  SolverType = 1
  Verbose = false
  _SolverType = 1
  _Version = 1
FEATURE [App::FeaturePython] Elements002  label="Elements_Piston"  # WARN: FeaturePython — macro-defined, semantics opaque (R4)
  Group = -> [Element006,Element007]
  GroupMode = 1
FEATURE [Part::FeaturePython] Assembly003  label="actuator_base_a"  # WARN: FeaturePython — macro-defined, semantics opaque (R4)
  AutoRelax = true
  BuildShape = 0
  Freeze = false
  Group = -> [Constraints003,Elements003,Parts003]
  GroupMode = 1
  Placement = pos=(4e-16,2.38418e-06,-20) rot=(0,0,1;0rad)
  SolverType = 1
  Verbose = false
  _SolverType = 1
  _Version = 1
FEATURE [App::FeaturePython] Elements003  label="Elements_Base"  # WARN: FeaturePython — macro-defined, semantics opaque (R4)
  Group = -> [Element004,Element005]
  GroupMode = 1
FEATURE [Part::FeaturePython] Assembly004  label="actuator_a"  # WARN: FeaturePython — macro-defined, semantics opaque (R4)
  AutoRelax = true
  BuildShape = 0
  Freeze = false
  Group = -> [Constraints004,Elements004,Parts004]
  GroupMode = 1
  SolverType = 1
  Verbose = false
  _SolverType = 1
  _Version = 1
FEATURE [App::FeaturePython] Constraints004  label="Constraints_Actuator"  # WARN: FeaturePython — macro-defined, semantics opaque (R4)
  Group = -> [Constraint,Constraint001,Constraint002,Constraint003]
  GroupMode = 1
  _Version = 1
FEATURE [App::FeaturePython] Elements004  label="Elements_Actuator"  # WARN: FeaturePython — macro-defined, semantics opaque (R4)
  Group = -> [_Element,_Element001,_Element002,_Element003,_Element004,Element008]
  GroupMode = 1
FEATURE [Part::FeaturePython] Parts004  label="Parts_Actuator"  # WARN: FeaturePython — macro-defined, semantics opaque (R4)
  Group = -> [Assembly003,Assembly002,Assembly]
  GroupMode = 0
FEATURE [Part::FeaturePython] Element  label="actuator_socket_hole"  # link proxy (typed FeaturePython)
  Detach = false
  LinkTransform = true
  LinkedObject = -> Body002 [Pad006.Sketch009.Edge6]
  _Parent = -> Elements
FEATURE [Part::FeaturePython] Element001  label="mount_hole"  # link proxy (typed FeaturePython)
  Detach = false
  LinkTransform = true
  LinkedObject = -> Body002 [Pocket003.Sketch011.Edge1]
  _Parent = -> Elements
FEATURE [Part::FeaturePython] Element003  label="mount_slot"  # link proxy (typed FeaturePython)
  Detach = false
  LinkTransform = true
  LinkedObject = -> Body002 [Pocket003.Sketch011.Edge2]
  _Parent = -> Elements
FEATURE [Part::FeaturePython] Element004  label="mount_bottom"  # link proxy (typed FeaturePython)
  Detach = false
  LinkTransform = true
  LinkedObject = -> Body [Hole.Sketch002.Edge1]
  Offset = pos=(0,0,-9) rot=(0,0,1;0rad)
  Placement = pos=(9,0,0) rot=(0,0,1;0rad)
  _Parent = -> Elements003
FEATURE [Part::FeaturePython] Element005  label="piston_hole"  # link proxy (typed FeaturePython)
  Detach = false
  LinkTransform = true
  LinkedObject = -> Body [Pocket.Sketch004.Edge1]
  _Parent = -> Elements003
FEATURE [Part::FeaturePython] Element006  label="piston_cylinder"  # link proxy (typed FeaturePython)
  Detach = false
  LinkTransform = true
  LinkedObject = -> Body001 [Pad003.Sketch005.Edge1]
  _Parent = -> Elements002
FEATURE [Part::FeaturePython] Element007  label="mount_top"  # link proxy (typed FeaturePython)
  Detach = false
  LinkTransform = true
  LinkedObject = -> Body001 [Pocket001.Sketch006.Edge1]
  _Parent = -> Elements002
FEATURE [App::FeaturePython] Constraint  label="Locked"  # WARN: FeaturePython — macro-defined, semantics opaque (R4)
  ConstraintType = 0
  Disabled = false
  Group = -> [ElementLink]
  GroupMode = 1
  _ConstraintType = 0
  _Parent = -> Constraints004
FEATURE [App::FeaturePython] ElementLink  label="_Element"  # link proxy (typed FeaturePython)
  LinkTransform = true
  LinkedObject = -> _Element
  _Parent = -> Constraint
FEATURE [Part::FeaturePython] _Element  # link proxy (typed FeaturePython)
  Detach = false
  LinkTransform = true
  LinkedObject = -> Assembly [1.$mount_hole.]
  _Parent = -> Elements004
FEATURE [App::FeaturePython] Constraint001  label="PlaneCoincident"  # WARN: FeaturePython — macro-defined, semantics opaque (R4)
  Angle = 0
  AnglePitch = 0
  AngleRoll = 0
  Cascade = false
  ConstraintType = 2
  Disabled = false
  Group = -> [ElementLink001,ElementLink002]
  GroupMode = 1
  LockAngle = false
  Multiply = false
  OffsetX = 0
  OffsetY = 0
  _ConstraintType = 35
  _Parent = -> Constraints004
FEATURE [App::FeaturePython] ElementLink001  label="_Element001"  # link proxy (typed FeaturePython)
  LinkTransform = true
  LinkedObject = -> _Element001
  _Parent = -> Constraint001
FEATURE [Part::FeaturePython] _Element001  # link proxy (typed FeaturePython)
  Detach = false
  LinkTransform = true
  LinkedObject = -> Assembly003 [1.$mount_bottom.]
  _Parent = -> Elements004
FEATURE [App::FeaturePython] ElementLink002  label="_Element002"  # link proxy (typed FeaturePython)
  LinkTransform = true
  LinkedObject = -> _Element002
  _Parent = -> Constraint001
FEATURE [Part::FeaturePython] _Element002  # link proxy (typed FeaturePython)
  Detach = false
  LinkTransform = true
  LinkedObject = -> Assembly [1.$actuator_socket_hole.]
  _Parent = -> Elements004
FEATURE [App::FeaturePython] Constraint002  label="PlaneCoincident001"  # WARN: FeaturePython — macro-defined, semantics opaque (R4)
  Angle = 0
  AnglePitch = 0
  AngleRoll = 0
  Cascade = false
  ConstraintType = 2
  Disabled = false
  Group = -> [ElementLink003,ElementLink004]
  GroupMode = 1
  LockAngle = true
  Multiply = false
  Offset = -500
  OffsetX = 0
  OffsetY = 0
  _ConstraintType = 35
  _Parent = -> Constraints004
FEATURE [App::FeaturePython] ElementLink003  label="_Element003"  # link proxy (typed FeaturePython)
  LinkTransform = true
  LinkedObject = -> _Element003
  _Parent = -> Constraint002
FEATURE [Part::FeaturePython] _Element003  # link proxy (typed FeaturePython)
  Detach = false
  LinkTransform = true
  LinkedObject = -> Assembly002 [1.$piston_cylinder.]
  _Parent = -> Elements004
FEATURE [App::FeaturePython] ElementLink004  label="_Element004"  # link proxy (typed FeaturePython)
  LinkTransform = true
  LinkedObject = -> _Element004
  _Parent = -> Constraint002
FEATURE [Part::FeaturePython] _Element004  # link proxy (typed FeaturePython)
  Detach = false
  LinkTransform = true
  LinkedObject = -> Assembly003 [1.$piston_hole.]
  _Parent = -> Elements004
FEATURE [Part::FeaturePython] Element008  label="mount_top"  # link proxy (typed FeaturePython)
  Detach = false
  LinkTransform = true
  LinkedObject = -> Assembly002 [1.$mount_top.]
  _Parent = -> Elements004
FEATURE [App::FeaturePython] Constraint003  label="MultiParallel"  # WARN: FeaturePython — macro-defined, semantics opaque (R4)
  Angle = 0
  AnglePitch = 0
  AngleRoll = 0
  ConstraintType = 6
  Disabled = false
  Group = -> [ElementLink005,ElementLink006]
  GroupMode = 1
  LockAngle = false
  _ConstraintType = 291
  _Parent = -> Constraints004
FEATURE [App::FeaturePython] ElementLink005  label="_Element003"  # link proxy (typed FeaturePython)
  LinkTransform = true
  LinkedObject = -> _Element003
  _Parent = -> Constraint003
FEATURE [App::FeaturePython] ElementLink006  label="_Element"  # link proxy (typed FeaturePython)
  LinkTransform = true
  LinkedObject = -> _Element
  _Parent = -> Constraint003
---- part ../parts/common/rail-450.FCStd = doc fcstd_040eeb14510a ----
FCSTD DOCUMENT  (FreeCAD 0.19R18044 (Git))
Label: rail-450
License: Public Domain
LicenseURL: http://en.wikipedia.org/wiki/Public_domain
objects: Part::FeaturePython×13, Sketcher::SketchObject×9, PartDesign::Pocket×6, App::FeaturePython×6, PartDesign::Pad×3, PartDesign::Body×3, PartDesign::LinearPattern×3, PartDesign::Line×2
note: 45 computed .brp shape members not serialized (recipe doc carries the construction recipe); baked Part::Feature solids carry a one-line shape summary decoded from their .brp

FEATURE [Sketcher::SketchObject] Sketch
  MapMode = 5
  Placement = pos=(0,0,0) rot=(1,0,0;1.5708rad)
  Support = -> [XZ_Plane]
  sketch-geometry (4):
    g0: LineSegment StartX=-22.5 StartY=12.7 StartZ=0 EndX=22.5 EndY=12.7 EndZ=0
    g1: LineSegment StartX=22.5 StartY=12.7 StartZ=0 EndX=22.5 EndY=0 EndZ=0
    g2: LineSegment StartX=22.5 StartY=0 StartZ=0 EndX=-22.5 EndY=0 EndZ=0
    g3: LineSegment StartX=-22.5 StartY=0 StartZ=0 EndX=-22.5 EndY=12.7 EndZ=0
  constraints (11):
    c: Coincident(g0,g1)
    c: Coincident(g1,g2)
    c: Coincident(g2,g3)
    c: Coincident(g3,g0)
    c: Horizontal(g2)
    c: Vertical(g1)
    c: Vertical(g3)
    c: PointOnObject(g1,g-1)
    c: Symmetric(g0,g0,g-2)
    c: Distance(g0) = 45
    c: Distance(g3) = 12.7
FEATURE [PartDesign::Pad] Pad
  ClaimChildren = false
  Length = 450
  Length2 = 100
  Placement = pos=(0,0,0) rot=(1,0,0;1.5708rad)
  Profile = -> Sketch
  Type = 0
FEATURE [Sketcher::SketchObject] Sketch001
  ExternalGeometry = -> [Pad]
  MapMode = 5
  Placement = pos=(0,-450,-9.9e-14) rot=(1,0,0;1.5708rad)
  Support = -> [Pad]
  sketch-geometry (8):
    g0: LineSegment StartX=-18.5 StartY=12.7 StartZ=0 EndX=-18.5 EndY=11.7 EndZ=0
    g1: LineSegment StartX=-18.5 StartY=11.7 StartZ=0 EndX=-21.5 EndY=11.7 EndZ=0
    g2: LineSegment StartX=-21.5 StartY=11.7 StartZ=0 EndX=-21.5 EndY=1 EndZ=0
    g3: LineSegment StartX=-21.5 StartY=1 StartZ=0 EndX=21.5 EndY=1 EndZ=0
    g4: LineSegment StartX=21.5 StartY=1 StartZ=0 EndX=21.5 EndY=11.7 EndZ=0
    g5: LineSegment StartX=21.5 StartY=11.7 StartZ=0 EndX=18.5 EndY=11.7 EndZ=0
    g6: LineSegment StartX=18.5 StartY=11.7 StartZ=0 EndX=18.5 EndY=12.7 EndZ=0
    g7: LineSegment StartX=18.5 StartY=12.7 StartZ=0 EndX=-18.5 EndY=12.7 EndZ=0
  constraints (23):
    c: Vertical(g0)
    c: Coincident(g0,g1)
    c: Horizontal(g1)
    c: Coincident(g1,g2)
    c: Vertical(g2)
    c: Coincident(g2,g3)
    c: Coincident(g3,g4)
    c: Vertical(g4)
    c: Coincident(g4,g5)
    c: Horizontal(g5)
    c: Coincident(g5,g6)
    c: Coincident(g6,g7)
    c: Coincident(g7,g0)
    c: PointOnObject(g6,g-4)
    c: DistanceX(g3,g-3) = 1
    c: DistanceY(g-3,g3) = 1
    c: DistanceY(g4,g-4) = 1
    c: Vertical(g6)
    c: Equal(g6,g0)
    c: Equal(g1,g5)
    c: Equal(g4,g2)
    c: Distance(g5) = 3
    c: Symmetric(g2,g3,g-2)
FEATURE [PartDesign::Pocket] Pocket
  BaseFeature = -> Pad
  ClaimChildren = false
  Length = 5
  Length2 = 100
  Placement = pos=(0,0,0) rot=(1,0,0;1.5708rad)
  Profile = -> Sketch001
  Type = 1
FEATURE [Sketcher::SketchObject] Sketch002
  MapMode = 5
  Placement = pos=(0,0,0) rot=(1,0,0;1.5708rad)
  Support = -> [XZ_Plane001]
  sketch-geometry (4):
    g0: LineSegment StartX=-17.5 StartY=12.7 StartZ=0 EndX=17.5 EndY=12.7 EndZ=0
    g1: LineSegment StartX=17.5 StartY=12.7 StartZ=0 EndX=17.5 EndY=2.7 EndZ=0
    g2: LineSegment StartX=17.5 StartY=2.7 StartZ=0 EndX=-17.5 EndY=2.7 EndZ=0
    g3: LineSegment StartX=-17.5 StartY=2.7 StartZ=0 EndX=-17.5 EndY=12.7 EndZ=0
  constraints (11):
    c: Coincident(g0,g1)
    c: Coincident(g1,g2)
    c: Coincident(g2,g3)
    c: Coincident(g3,g0)
    c: Horizontal(g2)
    c: Vertical(g1)
    c: Vertical(g3)
    c: Symmetric(g0,g0,g-2)
    c: Distance(g0) = 35
    c: DistanceY(g-1,g2) = 2.7
    c: Distance(g3) = 10
FEATURE [PartDesign::Pad] Pad001
  ClaimChildren = false
  Length = 450
  Length2 = 100
  Placement = pos=(0,0,0) rot=(1,0,0;1.5708rad)
  Profile = -> Sketch002
  Type = 0
FEATURE [Sketcher::SketchObject] Sketch003
  ExternalGeometry = -> [Pad001]
  MapMode = 5
  Placement = pos=(0,-450,-9.9e-14) rot=(1,0,0;1.5708rad)
  Support = -> [Pad001]
  sketch-geometry (8):
    g0: LineSegment StartX=-13.5 StartY=12.7 StartZ=0 EndX=-13.5 EndY=11.7 EndZ=0
    g1: LineSegment StartX=-13.5 StartY=11.7 StartZ=0 EndX=-16.5 EndY=11.7 EndZ=0
    g2: LineSegment StartX=-16.5 StartY=11.7 StartZ=0 EndX=-16.5 EndY=3.7 EndZ=0
    g3: LineSegment StartX=-16.5 StartY=3.7 StartZ=0 EndX=16.5 EndY=3.7 EndZ=0
    g4: LineSegment StartX=16.5 StartY=3.7 StartZ=0 EndX=16.5 EndY=11.7 EndZ=0
    g5: LineSegment StartX=16.5 StartY=11.7 StartZ=0 EndX=13.5 EndY=11.7 EndZ=0
    g6: LineSegment StartX=13.5 StartY=11.7 StartZ=0 EndX=13.5 EndY=12.7 EndZ=0
    g7: LineSegment StartX=13.5 StartY=12.7 StartZ=0 EndX=-13.5 EndY=12.7 EndZ=0
  constraints (23):
    c: PointOnObject(g0,g-3)
    c: Vertical(g0)
    c: Coincident(g0,g1)
    c: Horizontal(g1)
    c: Coincident(g1,g2)
    c: Vertical(g2)
    c: Coincident(g2,g3)
    c: Coincident(g3,g4)
    c: Vertical(g4)
    c: Coincident(g4,g5)
    c: Horizontal(g5)
    c: Coincident(g5,g6)
    c: PointOnObject(g6,g-3)
    c: Vertical(g6)
    c: Coincident(g6,g7)
    c: Coincident(g7,g0)
    c: Equal(g0,g6)
    c: Symmetric(g3,g2,g-2)
    c: Equal(g5,g1)
    c: DistanceX(g3,g-4) = 1
    c: DistanceY(g-4,g3) = 1
    c: DistanceY(g4,g-3) = 1
    c: Distance(g5) = 3
FEATURE [PartDesign::Pocket] Pocket001
  BaseFeature = -> Pad001
  ClaimChildren = false
  Length = 5
  Length2 = 100
  Placement = pos=(0,0,0) rot=(1,0,0;1.5708rad)
  Profile = -> Sketch003
  Type = 1
FEATURE [PartDesign::Body] Body001  label="rail 2"
  Group = -> [Sketch002,Pad001,Sketch003,Pocket001]
  Origin = -> Origin001
  SingleSolid = true
  Tip = -> Pocket001
FEATURE [Sketcher::SketchObject] Sketch004
  MapMode = 5
  Placement = pos=(0,0,0) rot=(1,0,0;1.5708rad)
  Support = -> [XZ_Plane002]
  sketch-geometry (4):
    g0: LineSegment StartX=-12.5 StartY=12.7 StartZ=0 EndX=12.5 EndY=12.7 EndZ=0
    g1: LineSegment StartX=12.5 StartY=12.7 StartZ=0 EndX=12.5 EndY=5.7 EndZ=0
    g2: LineSegment StartX=12.5 StartY=5.7 StartZ=0 EndX=-12.5 EndY=5.7 EndZ=0
    g3: LineSegment StartX=-12.5 StartY=5.7 StartZ=0 EndX=-12.5 EndY=12.7 EndZ=0
  constraints (11):
    c: Coincident(g0,g1)
    c: Coincident(g1,g2)
    c: Coincident(g2,g3)
    c: Coincident(g3,g0)
    c: Horizontal(g2)
    c: Vertical(g1)
    c: Vertical(g3)
    c: Symmetric(g0,g0,g-2)
    c: Distance(g0) = 25
    c: Distance(g3) = 7
    c: DistanceY(g-1,g0) = 12.7
FEATURE [PartDesign::Pad] Pad002
  ClaimChildren = false
  Length = 450
  Length2 = 100
  Placement = pos=(0,0,0) rot=(1,0,0;1.5708rad)
  Profile = -> Sketch004
  Type = 0
FEATURE [Sketcher::SketchObject] Sketch005
  ExternalGeometry = -> [Pad002]
  MapMode = 5
  Placement = pos=(0,-450,-9.9e-14) rot=(1,0,0;1.5708rad)
  Support = -> [Pad002]
  sketch-geometry (8):
    g0: LineSegment StartX=-11.5 StartY=11.7 StartZ=0 EndX=11.5 EndY=11.7 EndZ=0
    g1: LineSegment StartX=11.5 StartY=11.7 StartZ=0 EndX=11.5 EndY=6.7 EndZ=0
    g2: LineSegment StartX=11.5 StartY=6.7 StartZ=0 EndX=8.5 EndY=6.7 EndZ=0
    g3: LineSegment StartX=8.5 StartY=6.7 StartZ=0 EndX=8.5 EndY=5.7 EndZ=0
    g4: LineSegment StartX=8.5 StartY=5.7 StartZ=0 EndX=-8.5 EndY=5.7 EndZ=0
    g5: LineSegment StartX=-8.5 StartY=5.7 StartZ=0 EndX=-8.5 EndY=6.7 EndZ=0
    g6: LineSegment StartX=-8.5 StartY=6.7 StartZ=0 EndX=-11.5 EndY=6.7 EndZ=0
    g7: LineSegment StartX=-11.5 StartY=6.7 StartZ=0 EndX=-11.5 EndY=11.7 EndZ=0
  constraints (23):
    c: Coincident(g0,g1)
    c: Vertical(g1)
    c: Coincident(g1,g2)
    c: Horizontal(g2)
    c: Coincident(g2,g3)
    c: Vertical(g3)
    c: Coincident(g3,g4)
    c: Horizontal(g4)
    c: Coincident(g4,g5)
    c: Vertical(g5)
    c: Coincident(g5,g6)
    c: Horizontal(g6)
    c: Coincident(g6,g7)
    c: Coincident(g7,g0)
    c: Vertical(g7)
    c: PointOnObject(g4,g-3)
    c: Equal(g3,g5)
    c: Equal(g2,g6)
    c: DistanceX(g1,g-3) = 1
    c: DistanceY(g-3,g1) = 1
    c: Symmetric(g0,g0,g-2)
    c: Distance(g1) = 5
    c: Distance(g2) = 3
FEATURE [PartDesign::Pocket] Pocket002
  BaseFeature = -> Pad002
  ClaimChildren = false
  Length = 5
  Length2 = 100
  Placement = pos=(0,0,0) rot=(1,0,0;1.5708rad)
  Profile = -> Sketch005
  Type = 1
FEATURE [Sketcher::SketchObject] Sketch009
  MapMode = 5
  Placement = pos=(0,0,1) rot=(0,0,1;3.14159rad)
  Support = -> [Pocket]
  sketch-geometry (12):
    g0: LineSegment StartX=11 StartY=57 StartZ=0 EndX=11 EndY=26.2 EndZ=0
    g1: ArcOfCircle CenterX=8.8 CenterY=26.2 CenterZ=0 NormalX=0 NormalY=0 NormalZ=1 AngleXU=0 Radius=2.2 StartAngle=4.71239 EndAngle=6.28319
    g2: LineSegment StartX=8.8 StartY=24 StartZ=0 EndX=-8.8 EndY=24 EndZ=0
    g3: ArcOfCircle CenterX=-8.8 CenterY=26.2 CenterZ=0 NormalX=0 NormalY=0 NormalZ=1 AngleXU=0 Radius=2.2 StartAngle=3.14159 EndAngle=4.71239
    g4: LineSegment StartX=-11 StartY=26.2 StartZ=0 EndX=-11 EndY=57 EndZ=0
    g5: ArcOfCircle CenterX=-9.3 CenterY=57 CenterZ=0 NormalX=0 NormalY=0 NormalZ=1 AngleXU=0 Radius=1.7 StartAngle=-1.8e-15 EndAngle=3.14159
    g6: LineSegment StartX=-7.6 StartY=57 StartZ=0 EndX=-7.6 EndY=30.1 EndZ=0
    g7: ArcOfCircle CenterX=-5.9 CenterY=30.1 CenterZ=0 NormalX=0 NormalY=0 NormalZ=1 AngleXU=0 Radius=1.7 StartAngle=3.14159 EndAngle=4.71239
    g8: LineSegment StartX=-5.9 StartY=28.4 StartZ=0 EndX=5.9 EndY=28.4 EndZ=0
    g9: ArcOfCircle CenterX=5.9 CenterY=30.1 CenterZ=0 NormalX=0 NormalY=0 NormalZ=1 AngleXU=0 Radius=1.7 StartAngle=4.71239 EndAngle=6.28319
    g10: LineSegment StartX=7.6 StartY=30.1 StartZ=0 EndX=7.6 EndY=57 EndZ=0
    g11: ArcOfCircle CenterX=9.3 CenterY=57 CenterZ=0 NormalX=0 NormalY=0 NormalZ=1 AngleXU=0 Radius=1.7 StartAngle=-1.8e-15 EndAngle=3.14159
  constraints (30):
    c: Vertical(g0)
    c: Tangent(g0,g1) = 1.5708
    c: Tangent(g1,g2) = 1.5708
    c: Tangent(g2,g3) = 1.5708
    c: Tangent(g3,g4) = 1.5708
    c: Tangent(g4,g5) = 1.5708
    c: Tangent(g5,g6) = 1.5708
    c: Tangent(g6,g7) = -1.5708
    c: Tangent(g7,g8) = -1.5708
    c: Tangent(g8,g9) = -1.5708
    c: Tangent(g9,g10) = -1.5708
    c: Tangent(g10,g11) = 1.5708
    c: Horizontal(g8)
    c: Vertical(g10)
    c: Vertical(g6)
    c: Coincident(g11,g0)
    c: Vertical(g4)
    c: Equal(g6,g10)
    c: Equal(g4,g0)
    c: Horizontal(g10,g0)
    c: Equal(g5,g11)
    c: Equal(g9,g7)
    c: Diameter(g11) = 3.4
    c: Diameter(g1) = 4.4
    c: Diameter(g9) = 3.4
    c: DistanceY(g2,g7) = 4.4
    c: Symmetric(g1,g2,g-2)
    c: DistanceX(g3,g0) = 22
    c: DistanceY(g1,g10) = 33
    c: DistanceY(g-1,g2) = 24
FEATURE [PartDesign::Pocket] Pocket003
  BaseFeature = -> Pocket
  ClaimChildren = false
  Length = 5
  Length2 = 100
  Placement = pos=(0,0,0) rot=(1,0,0;1.5708rad)
  Profile = -> Sketch009
  Type = 1
FEATURE [PartDesign::LinearPattern] LinearPattern
  BaseFeature = -> Pocket003
  CopyShape = true
  Direction = -> Y_Axis
  Length = 65
  Occurrences = 2
  OriginalSubs = -> [Pocket003]
  Originals = -> [Pocket003]
  Placement = pos=(0,0,0) rot=(1,0,0;1.5708rad)
  Reversed = true
  SubTransform = true
FEATURE [PartDesign::LinearPattern] LinearPattern001
  BaseFeature = -> LinearPattern
  CopyShape = true
  Direction = -> Y_Axis
  Length = 320
  Occurrences = 3
  OriginalSubs = -> [Pocket003]
  Originals = -> [Pocket003]
  Placement = pos=(0,0,0) rot=(1,0,0;1.5708rad)
  Reversed = true
  SubTransform = true
FEATURE [PartDesign::LinearPattern] LinearPattern002
  BaseFeature = -> LinearPattern001
  CopyShape = true
  Direction = -> Y_Axis
  Length = 257
  Occurrences = 2
  OriginalSubs = -> [Pocket003]
  Originals = -> [Pocket003]
  Placement = pos=(0,0,0) rot=(1,0,0;1.5708rad)
  Reversed = true
  SubTransform = true
FEATURE [Sketcher::SketchObject] Sketch010
  ExternalGeometry = -> [LinearPattern002]
  MapMode = 5
  Placement = pos=(0,0,1) rot=(0,0,1;3.14159rad)
  Support = -> [LinearPattern002]
  sketch-geometry (57):
    g0: Circle CenterX=0 CenterY=6 CenterZ=0 NormalX=0 NormalY=0 NormalZ=1 AngleXU=0 Radius=2.4
    g1: Circle CenterX=0 CenterY=430 CenterZ=0 NormalX=0 NormalY=0 NormalZ=1 AngleXU=0 Radius=2.4
    g2: Circle CenterX=0 CenterY=35.1 CenterZ=0 NormalX=0 NormalY=0 NormalZ=1 AngleXU=0 Radius=2.2
    g3: Circle CenterX=0 CenterY=100.1 CenterZ=0 NormalX=0 NormalY=0 NormalZ=1 AngleXU=0 Radius=2.2
    g4: Circle CenterX=0 CenterY=195.1 CenterZ=0 NormalX=0 NormalY=0 NormalZ=1 AngleXU=0 Radius=2.2
    g5: Circle CenterX=0 CenterY=292.1 CenterZ=0 NormalX=0 NormalY=0 NormalZ=1 AngleXU=0 Radius=2.2
    g6: Circle CenterX=0 CenterY=355.1 CenterZ=0 NormalX=0 NormalY=0 NormalZ=1 AngleXU=0 Radius=2.2
    g7: Circle CenterX=0 CenterY=272.4 CenterZ=0 NormalX=0 NormalY=0 NormalZ=1 AngleXU=0 Radius=2.2
    g8: Circle CenterX=0 CenterY=179.4 CenterZ=0 NormalX=0 NormalY=0 NormalZ=1 AngleXU=0 Radius=2.2
    g9: ArcOfCircle CenterX=0 CenterY=48.8 CenterZ=0 NormalX=0 NormalY=0 NormalZ=1 AngleXU=0 Radius=2.2 StartAngle=3.14159 EndAngle=6.28319
    g10: ArcOfCircle CenterX=-2e-16 CenterY=53.2 CenterZ=0 NormalX=0 NormalY=0 NormalZ=1 AngleXU=0 Radius=2.2 StartAngle=-9e-16 EndAngle=3.14159
    g11: LineSegment StartX=2.2 StartY=48.8 StartZ=0 EndX=2.2 EndY=53.2 EndZ=0
    g12: LineSegment StartX=-2.2 StartY=48.8 StartZ=0 EndX=-2.2 EndY=53.2 EndZ=0
    g13: ArcOfCircle CenterX=0 CenterY=64.8 CenterZ=0 NormalX=0 NormalY=0 NormalZ=1 AngleXU=0 Radius=2.2 StartAngle=3.14159 EndAngle=6.28319
    g14: ArcOfCircle CenterX=0 CenterY=69.2 CenterZ=0 NormalX=0 NormalY=0 NormalZ=1 AngleXU=0 Radius=2.2 StartAngle=1.2e-15 EndAngle=3.14159
    g15: LineSegment StartX=2.2 StartY=64.8 StartZ=0 EndX=2.2 EndY=69.2 EndZ=0
    g16: LineSegment StartX=-2.2 StartY=64.8 StartZ=0 EndX=-2.2 EndY=69.2 EndZ=0
    g17: ArcOfCircle CenterX=0 CenterY=113.8 CenterZ=0 NormalX=0 NormalY=0 NormalZ=1 AngleXU=0 Radius=2.2 StartAngle=3.14159 EndAngle=6.28319
    g18: ArcOfCircle CenterX=2e-16 CenterY=118.2 CenterZ=0 NormalX=0 NormalY=0 NormalZ=1 AngleXU=0 Radius=2.2 StartAngle=9e-16 EndAngle=3.14159
    g19: LineSegment StartX=2.2 StartY=113.8 StartZ=0 EndX=2.2 EndY=118.2 EndZ=0
    g20: LineSegment StartX=-2.2 StartY=113.8 StartZ=0 EndX=-2.2 EndY=118.2 EndZ=0
    g21: ArcOfCircle CenterX=0 CenterY=129.8 CenterZ=0 NormalX=0 NormalY=0 NormalZ=1 AngleXU=0 Radius=2.2 StartAngle=3.14159 EndAngle=6.28319
    g22: ArcOfCircle CenterX=1e-16 CenterY=134.2 CenterZ=0 NormalX=0 NormalY=0 NormalZ=1 AngleXU=0 Radius=2.2 StartAngle=0 EndAngle=3.14159
    g23: LineSegment StartX=2.2 StartY=129.8 StartZ=0 EndX=2.2 EndY=134.2 EndZ=0
    g24: LineSegment StartX=-2.2 StartY=129.8 StartZ=0 EndX=-2.2 EndY=134.2 EndZ=0
    g25: ArcOfCircle CenterX=0 CenterY=208.8 CenterZ=0 NormalX=0 NormalY=0 NormalZ=1 AngleXU=0 Radius=2.2 StartAngle=3.14159 EndAngle=6.28319
    g26: ArcOfCircle CenterX=2e-16 CenterY=213.2 CenterZ=0 NormalX=0 NormalY=0 NormalZ=1 AngleXU=0 Radius=2.2 StartAngle=-4.4e-15 EndAngle=3.14159
    g27: LineSegment StartX=2.2 StartY=208.8 StartZ=0 EndX=2.2 EndY=213.2 EndZ=0
    g28: LineSegment StartX=-2.2 StartY=208.8 StartZ=0 EndX=-2.2 EndY=213.2 EndZ=0
    g29: ArcOfCircle CenterX=0 CenterY=224.8 CenterZ=0 NormalX=0 NormalY=0 NormalZ=1 AngleXU=0 Radius=2.2 StartAngle=3.14159 EndAngle=6.28319
    g30: ArcOfCircle CenterX=0 CenterY=229.2 CenterZ=0 NormalX=0 NormalY=0 NormalZ=1 AngleXU=0 Radius=2.2 StartAngle=1.1e-15 EndAngle=3.14159
    g31: LineSegment StartX=2.2 StartY=224.8 StartZ=0 EndX=2.2 EndY=229.2 EndZ=0
    g32: LineSegment StartX=-2.2 StartY=224.8 StartZ=0 EndX=-2.2 EndY=229.2 EndZ=0
    g33: ArcOfCircle CenterX=0 CenterY=305.8 CenterZ=0 NormalX=0 NormalY=0 NormalZ=1 AngleXU=0 Radius=2.2 StartAngle=3.14159 EndAngle=6.28319
    g34: ArcOfCircle CenterX=-1e-16 CenterY=310.2 CenterZ=0 NormalX=0 NormalY=0 NormalZ=1 AngleXU=0 Radius=2.2 StartAngle=-1.15e-14 EndAngle=3.14159
    g35: LineSegment StartX=2.2 StartY=305.8 StartZ=0 EndX=2.2 EndY=310.2 EndZ=0
    g36: LineSegment StartX=-2.2 StartY=305.8 StartZ=0 EndX=-2.2 EndY=310.2 EndZ=0
    g37: ArcOfCircle CenterX=0 CenterY=321.8 CenterZ=0 NormalX=0 NormalY=0 NormalZ=1 AngleXU=0 Radius=2.2 StartAngle=3.14159 EndAngle=6.28319
    g38: ArcOfCircle CenterX=-1e-16 CenterY=326.2 CenterZ=0 NormalX=0 NormalY=0 NormalZ=1 AngleXU=0 Radius=2.2 StartAngle=-9e-16 EndAngle=3.14159
    g39: LineSegment StartX=2.2 StartY=321.8 StartZ=0 EndX=2.2 EndY=326.2 EndZ=0
    g40: LineSegment StartX=-2.2 StartY=321.8 StartZ=0 EndX=-2.2 EndY=326.2 EndZ=0
    g41: ArcOfCircle CenterX=0 CenterY=368.8 CenterZ=0 NormalX=0 NormalY=0 NormalZ=1 AngleXU=0 Radius=2.2 StartAngle=3.14159 EndAngle=6.28319
    g42: ArcOfCircle CenterX=-2.4482e-12 CenterY=373.2 CenterZ=0 NormalX=0 NormalY=0 NormalZ=1 AngleXU=0 Radius=2.2 StartAngle=-4.254e-13 EndAngle=3.14159
    g43: LineSegment StartX=2.2 StartY=368.8 StartZ=0 EndX=2.2 EndY=373.2 EndZ=0
    g44: LineSegment StartX=-2.2 StartY=368.8 StartZ=0 EndX=-2.2 EndY=373.2 EndZ=0
    g45: ArcOfCircle CenterX=0 CenterY=384.8 CenterZ=0 NormalX=0 NormalY=0 NormalZ=1 AngleXU=0 Radius=2.2 StartAngle=3.14159 EndAngle=6.28319
    g46: ArcOfCircle CenterX=2.4481e-12 CenterY=389.2 CenterZ=0 NormalX=0 NormalY=0 NormalZ=1 AngleXU=0 Radius=2.2 StartAngle=-2.7e-15 EndAngle=3.14159
    g47: LineSegment StartX=2.2 StartY=384.8 StartZ=0 EndX=2.2 EndY=389.2 EndZ=0
    g48: LineSegment StartX=-2.2 StartY=384.8 StartZ=0 EndX=-2.2 EndY=389.2 EndZ=0
    g49: LineSegment StartX=21 StartY=4 StartZ=0 EndX=16 EndY=4 EndZ=0
    g50: LineSegment StartX=16 StartY=4 StartZ=0 EndX=16 EndY=8 EndZ=0
    g51: LineSegment StartX=16 StartY=8 StartZ=0 EndX=21 EndY=8 EndZ=0
    g52: LineSegment StartX=21 StartY=8 StartZ=0 EndX=21 EndY=4 EndZ=0
    g53: LineSegment StartX=-16 StartY=4 StartZ=0 EndX=-21 EndY=4 EndZ=0
    g54: LineSegment StartX=-21 StartY=4 StartZ=0 EndX=-21 EndY=8 EndZ=0
    g55: LineSegment StartX=-21 StartY=8 StartZ=0 EndX=-16 EndY=8 EndZ=0
    g56: LineSegment StartX=-16 StartY=8 StartZ=0 EndX=-16 EndY=4 EndZ=0
  constraints (150):
    c: PointOnObject(g0,g-2)
    c: Equal(g1,g0)
    c: Diameter(g0) = 4.8
    c: DistanceY(g-1,g0) = 6
    c: DistanceY(g-1,g1) = 430
    c: PointOnObject(g1,g-2)
    c: PointOnObject(g2,g-2)
    c: PointOnObject(g3,g-2)
    c: PointOnObject(g4,g-2)
    c: PointOnObject(g5,g-2)
    c: PointOnObject(g6,g-2)
    c: PointOnObject(g7,g-2)
    c: PointOnObject(g8,g-2)
    c: Equal(g3,g8)
    c: Equal(g8,g4)
    c: Equal(g4,g7)
    c: Equal(g7,g5)
    c: Equal(g5,g6)
    c: Diameter(g2) = 4.4
    c: DistanceY(g-7,g6) = 6.7
    c: DistanceY(g-6,g5) = 6.7
    c: DistanceY(g-5,g4) = 6.7
    c: DistanceY(g-4,g3) = 6.7
    c: DistanceY(g-3,g2) = 6.7
    c: Equal(g2,g3)
    c: DistanceY(g7,g-6) = 13
    c: DistanceY(g8,g-5) = 9
    c: Tangent(g9,g12) = 1.5708
    c: Tangent(g9,g11) = -1.5708
    c: Tangent(g11,g10) = -1.5708
    c: Tangent(g12,g10) = 1.5708
    c: Vertical(g11)
    c: Equal(g9,g10)
    c: PointOnObject(g9,g-2)
    c: Diameter(g9) = 4.4
    c: Distance(g12) = 4.4
    c: DistanceY(g-3,g9) = 20.4
    c: Tangent(g13,g16) = 1.5708
    c: Tangent(g13,g15) = -1.5708
    c: Tangent(g15,g14) = -1.5708
    c: Tangent(g16,g14) = 1.5708
    c: Vertical(g15)
    c: Equal(g13,g14)
    c: PointOnObject(g13,g-2)
    c: Equal(g12,g16)
    c: Equal(g13,g10)
    c: DistanceY(g10,g13) = 11.6
    c: Tangent(g17,g20) = 1.5708
    c: Tangent(g17,g19) = -1.5708
    c: Tangent(g19,g18) = -1.5708
    c: Tangent(g20,g18) = 1.5708
    c: Vertical(g19)
    c: Equal(g17,g18)
    c: PointOnObject(g17,g-2)
    c: Equal(g20,g16)
    c: Equal(g17,g13)
    c: DistanceY(g-4,g17) = 20.4
    c: Tangent(g21,g24) = 1.5708
    c: Tangent(g21,g23) = -1.5708
    c: Tangent(g23,g22) = -1.5708
    c: Tangent(g24,g22) = 1.5708
    c: Vertical(g23)
    c: Equal(g21,g22)
    c: PointOnObject(g21,g-2)
    c: Equal(g24,g20)
    c: Equal(g17,g21)
    c: DistanceY(g18,g21) = 11.6
    c: Tangent(g25,g28) = 1.5708
    c: Tangent(g25,g27) = -1.5708
    c: Tangent(g27,g26) = -1.5708
    c: Tangent(g28,g26) = 1.5708
    c: Vertical(g27)
    c: Equal(g25,g26)
    c: PointOnObject(g25,g-2)
    c: Equal(g28,g24)
    c: Equal(g25,g21)
    c: DistanceY(g-5,g25) = 20.4
    c: Tangent(g29,g32) = 1.5708
    c: Tangent(g29,g31) = -1.5708
    c: Tangent(g31,g30) = -1.5708
    c: Tangent(g32,g30) = 1.5708
    c: Vertical(g31)
    c: Equal(g29,g30)
    c: PointOnObject(g29,g-2)
    c: Equal(g32,g28)
    c: Equal(g29,g25)
    c: DistanceY(g26,g29) = 11.6
    c: Tangent(g33,g36) = 1.5708
    c: Tangent(g33,g35) = -1.5708
    c: Tangent(g35,g34) = -1.5708
    c: Tangent(g36,g34) = 1.5708
    c: Vertical(g35)
    c: Equal(g33,g34)
    c: PointOnObject(g33,g-2)
    c: Equal(g32,g36)
    c: Equal(g33,g30)
    c: DistanceY(g-6,g33) = 20.4
    c: Tangent(g37,g40) = 1.5708
    c: Tangent(g37,g39) = -1.5708
    c: Tangent(g39,g38) = -1.5708
    c: Tangent(g40,g38) = 1.5708
    c: Vertical(g39)
    c: Equal(g37,g38)
    c: PointOnObject(g37,g-2)
    c: Equal(g40,g36)
    c: Equal(g37,g34)
    c: DistanceY(g34,g37) = 11.6
    c: Tangent(g41,g44) = 1.5708
    c: Tangent(g41,g43) = -1.5708
    c: Tangent(g43,g42) = -1.5708
    c: Tangent(g44,g42) = 1.5708
    c: Vertical(g43)
    c: Equal(g41,g42)
    c: PointOnObject(g41,g-2)
    c: Equal(g44,g40)
    c: Equal(g41,g38)
    c: DistanceY(g-7,g41) = 20.4
    c: Tangent(g45,g48) = 1.5708
    c: Tangent(g45,g47) = -1.5708
    c: Tangent(g47,g46) = -1.5708
    c: Tangent(g48,g46) = 1.5708
    c: Vertical(g47)
    c: Equal(g45,g46)
    c: PointOnObject(g45,g-2)
    c: Equal(g48,g44)
    c: Equal(g45,g42)
    c: DistanceY(g42,g45) = 11.6
    c: Coincident(g49,g50)
    c: Coincident(g50,g51)
    c: Coincident(g51,g52)
    c: Coincident(g52,g49)
    c: Horizontal(g49)
    c: Horizontal(g51)
    c: Vertical(g50)
    c: Vertical(g52)
    c: Coincident(g53,g54)
    c: Coincident(g54,g55)
    c: Coincident(g55,g56)
    c: Coincident(g56,g53)
    c: Horizontal(g53)
    c: Horizontal(g55)
    c: Vertical(g54)
    c: Vertical(g56)
    c: Equal(g56,g50)
    c: Equal(g53,g49)
    c: Symmetric(g53,g49,g-2)
    c: Distance(g54) = 4
    c: Distance(g53) = 5
    c: DistanceY(g-1,g53) = 4
    c: DistanceX(g53,g-1) = 21
FEATURE [PartDesign::Pocket] Pocket004
  BaseFeature = -> LinearPattern002
  ClaimChildren = false
  Length = 5
  Length2 = 100
  Placement = pos=(0,0,0) rot=(1,0,0;1.5708rad)
  Profile = -> Sketch010
  Type = 1
FEATURE [Sketcher::SketchObject] Sketch011
  MapMode = 5
  Placement = pos=(0,0,12.7) rot=(0,0,1;3.14159rad)
  Support = -> [Pocket002]
  sketch-geometry (36):
    g0: Circle CenterX=0 CenterY=25 CenterZ=0 NormalX=0 NormalY=0 NormalZ=1 AngleXU=0 Radius=2.2
    g1: ArcOfCircle CenterX=2.2 CenterY=35 CenterZ=0 NormalX=0 NormalY=0 NormalZ=1 AngleXU=0 Radius=2.2 StartAngle=4.71239 EndAngle=7.85398
    g2: ArcOfCircle CenterX=-2.2 CenterY=35 CenterZ=0 NormalX=0 NormalY=0 NormalZ=1 AngleXU=0 Radius=2.2 StartAngle=1.5708 EndAngle=4.71239
    g3: LineSegment StartX=2.2 StartY=37.2 StartZ=0 EndX=-2.2 EndY=37.2 EndZ=0
    g4: LineSegment StartX=2.2 StartY=32.8 StartZ=0 EndX=-2.2 EndY=32.8 EndZ=0
    g5: ArcOfCircle CenterX=0 CenterY=50 CenterZ=0 NormalX=0 NormalY=0 NormalZ=1 AngleXU=0 Radius=2.2 StartAngle=-9e-16 EndAngle=3.14159
    g6: ArcOfCircle CenterX=-2e-16 CenterY=45.6 CenterZ=0 NormalX=0 NormalY=0 NormalZ=1 AngleXU=0 Radius=2.2 StartAngle=3.14159 EndAngle=6.28319
    g7: LineSegment StartX=-2.2 StartY=50 StartZ=0 EndX=-2.2 EndY=45.6 EndZ=0
    g8: LineSegment StartX=2.2 StartY=50 StartZ=0 EndX=2.2 EndY=45.6 EndZ=0
    g9: Circle CenterX=0 CenterY=185 CenterZ=0 NormalX=0 NormalY=0 NormalZ=1 AngleXU=0 Radius=2.2
    g10: ArcOfCircle CenterX=2.2 CenterY=195 CenterZ=0 NormalX=0 NormalY=0 NormalZ=1 AngleXU=0 Radius=2.2 StartAngle=4.71239 EndAngle=7.85398
    g11: ArcOfCircle CenterX=-2.2 CenterY=195 CenterZ=0 NormalX=0 NormalY=0 NormalZ=1 AngleXU=0 Radius=2.2 StartAngle=1.5708 EndAngle=4.71239
    g12: LineSegment StartX=2.2 StartY=197.2 StartZ=0 EndX=-2.2 EndY=197.2 EndZ=0
    g13: LineSegment StartX=2.2 StartY=192.8 StartZ=0 EndX=-2.2 EndY=192.8 EndZ=0
    g14: ArcOfCircle CenterX=0 CenterY=205.6 CenterZ=0 NormalX=0 NormalY=0 NormalZ=1 AngleXU=0 Radius=2.2 StartAngle=3.14159 EndAngle=6.28319
    g15: ArcOfCircle CenterX=0 CenterY=210 CenterZ=0 NormalX=0 NormalY=0 NormalZ=1 AngleXU=0 Radius=2.2 StartAngle=2.8e-15 EndAngle=3.14159
    g16: LineSegment StartX=2.2 StartY=205.6 StartZ=0 EndX=2.2 EndY=210 EndZ=0
    g17: LineSegment StartX=-2.2 StartY=205.6 StartZ=0 EndX=-2.2 EndY=210 EndZ=0
    g18: LineSegment [constr] StartX=0 StartY=35 StartZ=0 EndX=0 EndY=25 EndZ=0
    g19: LineSegment [constr] StartX=2.2 StartY=35 StartZ=0 EndX=0 EndY=35 EndZ=0
    g20: LineSegment [constr] StartX=0 StartY=35 StartZ=0 EndX=-2e-16 EndY=45.6 EndZ=0
    g21: LineSegment [constr] StartX=2.2 StartY=195 StartZ=0 EndX=0 EndY=195 EndZ=0
    g22: LineSegment [constr] StartX=0 StartY=185 StartZ=0 EndX=0 EndY=195 EndZ=0
    g23: LineSegment [constr] StartX=0 StartY=195 StartZ=0 EndX=0 EndY=205.6 EndZ=0
    g24: Circle CenterX=0 CenterY=377 CenterZ=0 NormalX=0 NormalY=0 NormalZ=1 AngleXU=0 Radius=2.2
    g25: ArcOfCircle CenterX=2.2 CenterY=387 CenterZ=0 NormalX=0 NormalY=0 NormalZ=1 AngleXU=0 Radius=2.2 StartAngle=4.71239 EndAngle=7.85398
    g26: ArcOfCircle CenterX=-2.2 CenterY=387 CenterZ=0 NormalX=0 NormalY=0 NormalZ=1 AngleXU=0 Radius=2.2 StartAngle=1.5708 EndAngle=4.71239
    g27: LineSegment StartX=2.2 StartY=389.2 StartZ=0 EndX=-2.2 EndY=389.2 EndZ=0
    g28: LineSegment StartX=2.2 StartY=384.8 StartZ=0 EndX=-2.2 EndY=384.8 EndZ=0
    g29: ArcOfCircle CenterX=0 CenterY=402 CenterZ=0 NormalX=0 NormalY=0 NormalZ=1 AngleXU=0 Radius=2.2 StartAngle=-7.1e-15 EndAngle=3.14159
    g30: ArcOfCircle CenterX=-1e-16 CenterY=397.6 CenterZ=0 NormalX=0 NormalY=0 NormalZ=1 AngleXU=0 Radius=2.2 StartAngle=3.14159 EndAngle=6.28319
    g31: LineSegment StartX=-2.2 StartY=402 StartZ=0 EndX=-2.2 EndY=397.6 EndZ=0
    g32: LineSegment StartX=2.2 StartY=402 StartZ=0 EndX=2.2 EndY=397.6 EndZ=0
    g33: LineSegment [constr] StartX=2.2 StartY=387 StartZ=0 EndX=0 EndY=387 EndZ=0
    g34: LineSegment [constr] StartX=0 StartY=377 StartZ=0 EndX=0 EndY=387 EndZ=0
    g35: LineSegment [constr] StartX=0 StartY=387 StartZ=0 EndX=-1e-16 EndY=397.6 EndZ=0
  constraints (89):
    c: PointOnObject(g0,g-2)
    c: Tangent(g1,g4) = 1.5708
    c: Tangent(g1,g3) = -1.5708
    c: Tangent(g3,g2) = -1.5708
    c: Tangent(g4,g2) = 1.5708
    c: Horizontal(g3)
    c: Tangent(g5,g8) = 1.5708
    c: Tangent(g5,g7) = -1.5708
    c: Tangent(g7,g6) = -1.5708
    c: Tangent(g8,g6) = 1.5708
    c: Vertical(g7)
    c: Equal(g5,g6)
    c: PointOnObject(g5,g-2)
    c: Equal(g4,g8)
    c: Equal(g2,g5)
    c: Symmetric(g2,g1,g-2)
    c: Diameter(g2) = 4.4
    c: Distance(g4) = 4.4
    c: Diameter(g0) = 4.4
    c: DistanceY(g-1,g0) = 25
    c: DistanceY(g-1,g2) = 35
    c: DistanceY(g5) = 50
    c: PointOnObject(g9,g-2)
    c: Tangent(g10,g13) = 1.5708
    c: Tangent(g10,g12) = -1.5708
    c: Tangent(g12,g11) = -1.5708
    c: Tangent(g13,g11) = 1.5708
    c: Horizontal(g12)
    c: Tangent(g14,g17) = 1.5708
    c: Tangent(g14,g16) = -1.5708
    c: Tangent(g16,g15) = -1.5708
    c: Tangent(g17,g15) = 1.5708
    c: Vertical(g16)
    c: Equal(g14,g15)
    c: Equal(g14,g11)
    c: Equal(g11,g10)
    c: Equal(g15,g5)
    c: Equal(g9,g0)
    c: Equal(g7,g17)
    c: Equal(g13,g3)
    c: PointOnObject(g18,g-2)
    c: Coincident(g18,g0)
    c: Coincident(g19,g1)
    c: Horizontal(g19)
    c: Coincident(g19,g18)
    c: Coincident(g20,g18)
    c: Coincident(g20,g6)
    c: PointOnObject(g21,g-2)
    c: Coincident(g21,g10)
    c: Horizontal(g21)
    c: DistanceY(g0,g9) = 160
    c: Equal(g21,g19)
    c: Coincident(g22,g9)
    c: Coincident(g22,g21)
    c: Coincident(g23,g21)
    c: Coincident(g23,g14)
    c: Vertical(g23)
    c: Equal(g23,g20)
    c: Equal(g18,g22)
    c: PointOnObject(g24,g-2)
    c: Tangent(g25,g28) = 1.5708
    c: Tangent(g25,g27) = -1.5708
    c: Tangent(g27,g26) = -1.5708
    c: Tangent(g28,g26) = 1.5708
    c: Horizontal(g27)
    c: Equal(g25,g26)
    c: Tangent(g29,g32) = 1.5708
    c: Tangent(g29,g31) = -1.5708
    c: Tangent(g31,g30) = -1.5708
    c: Tangent(g32,g30) = 1.5708
    c: Vertical(g31)
    c: Equal(g29,g30)
    c: PointOnObject(g29,g-2)
    c: Equal(g30,g26)
    c: Equal(g26,g5)
    c: Equal(g24,g0)
    c: Equal(g28,g4)
    c: Equal(g7,g31)
    c: Coincident(g33,g25)
    c: PointOnObject(g33,g-2)
    c: Horizontal(g33)
    c: Coincident(g34,g24)
    c: Coincident(g34,g33)
    c: Coincident(g35,g33)
    c: Coincident(g35,g30)
    c: Equal(g34,g18)
    c: Equal(g20,g35)
    c: Equal(g33,g19)
    c: DistanceY(g0,g24) = 352
FEATURE [PartDesign::Pocket] Pocket005
  BaseFeature = -> Pocket002
  ClaimChildren = false
  Length = 5
  Length2 = 100
  Placement = pos=(0,0,0) rot=(1,0,0;1.5708rad)
  Profile = -> Sketch011
  Type = 1
FEATURE [App::FeaturePython] Constraints  # WARN: FeaturePython — macro-defined, semantics opaque (R4)
  GroupMode = 1
  _Version = 1
FEATURE [App::FeaturePython] Constraints001  # WARN: FeaturePython — macro-defined, semantics opaque (R4)
  GroupMode = 1
  _Version = 1
FEATURE [App::FeaturePython] Elements001  # WARN: FeaturePython — macro-defined, semantics opaque (R4)
  GroupMode = 1
FEATURE [Part::FeaturePython] Parts001  # WARN: FeaturePython — macro-defined, semantics opaque (R4)
  Group = -> [Origin004,Body001]
  GroupMode = 0
FEATURE [Part::FeaturePython] Assembly001  label="rail middle"  # WARN: FeaturePython — macro-defined, semantics opaque (R4)
  AutoRelax = true
  BuildShape = 0
  Freeze = false
  Group = -> [Constraints001,Elements001,Parts001]
  GroupMode = 1
  SolverType = 1
  Verbose = false
  _SolverType = 1
  _Version = 1
FEATURE [App::FeaturePython] Constraints002  # WARN: FeaturePython — macro-defined, semantics opaque (R4)
  GroupMode = 1
  _Version = 1
FEATURE [PartDesign::Line] DatumLine
  AttacherType = Attacher::AttachEngineLine
  AttachmentOffset = pos=(6.35,0,0) rot=(0,0,1;0rad)
  MapMode = 16
  Placement = pos=(-4e-16,4e-16,6.35) rot=(0.57735,0.57735,0.57735;4.18879rad)
  Support = -> [Y_Axis]
FEATURE [PartDesign::Body] Body  label="rail 1"
  Group = -> [Sketch,Pad,Sketch001,Pocket,Sketch009,Pocket003,LinearPattern,LinearPattern001,LinearPattern002,Sketch010,Pocket004,DatumLine]
  Origin = -> Origin
  SingleSolid = true
  Tip = -> Pocket004
FEATURE [Part::FeaturePython] Parts  # WARN: FeaturePython — macro-defined, semantics opaque (R4)
  Group = -> [Origin003,Body]
  GroupMode = 0
FEATURE [PartDesign::Line] DatumLine001
  AttacherType = Attacher::AttachEngineLine
  AttachmentOffset = pos=(6.35,0,0) rot=(0,0,1;0rad)
  MapMode = 16
  Placement = pos=(-4e-16,4e-16,6.35) rot=(0.57735,0.57735,0.57735;4.18879rad)
  Support = -> [Y_Axis002]
FEATURE [PartDesign::Body] Body002  label="rail 3"
  Group = -> [Sketch004,Pad002,Sketch005,Pocket002,Sketch011,Pocket005,DatumLine001]
  Origin = -> Origin002
  SingleSolid = true
  Tip = -> Pocket005
FEATURE [Part::FeaturePython] Parts002  # WARN: FeaturePython — macro-defined, semantics opaque (R4)
  Group = -> [Origin005,Body002]
  GroupMode = 0
FEATURE [Part::FeaturePython] Assembly  label="rail bottom"  # WARN: FeaturePython — macro-defined, semantics opaque (R4)
  AutoRelax = true
  BuildShape = 0
  Freeze = false
  Group = -> [Constraints,Elements,Parts]
  GroupMode = 1
  SolverType = 1
  Verbose = false
  _SolverType = 1
  _Version = 1
FEATURE [App::FeaturePython] Elements  # WARN: FeaturePython — macro-defined, semantics opaque (R4)
  Group = -> [Element003,Element004,Element005]
  GroupMode = 1
FEATURE [Part::FeaturePython] Assembly002  label="rail top"  # WARN: FeaturePython — macro-defined, semantics opaque (R4)
  AutoRelax = true
  BuildShape = 0
  Freeze = false
  Group = -> [Constraints002,Elements002,Parts002]
  GroupMode = 1
  SolverType = 1
  Verbose = false
  _SolverType = 1
  _Version = 1
FEATURE [App::FeaturePython] Elements002  # WARN: FeaturePython — macro-defined, semantics opaque (R4)
  Group = -> [Element,Element001,Element002,Element006]
  GroupMode = 1
FEATURE [Part::FeaturePython] Element  label="mount_top"  # link proxy (typed FeaturePython)
  Detach = false
  LinkTransform = true
  LinkedObject = -> Body002 [Pocket005.Sketch011.Edge1]
  _Parent = -> Elements002
FEATURE [Part::FeaturePython] Element001  label="mount_middle"  # link proxy (typed FeaturePython)
  Detach = false
  LinkTransform = true
  LinkedObject = -> Body002 [Pocket005.Sketch011.Edge10]
  _Parent = -> Elements002
FEATURE [Part::FeaturePython] Element002  label="mount_bottom"  # link proxy (typed FeaturePython)
  Detach = false
  LinkTransform = true
  LinkedObject = -> Body002 [Pocket005.Sketch011.Edge19]
  _Parent = -> Elements002
FEATURE [Part::FeaturePython] Element003  label="mount_top"  # link proxy (typed FeaturePython)
  Detach = false
  LinkTransform = true
  LinkedObject = -> Body [Pocket004.Sketch010.Edge1]
  _Parent = -> Elements
FEATURE [Part::FeaturePython] Element004  label="mount_bottom"  # link proxy (typed FeaturePython)
  Detach = false
  LinkTransform = true
  LinkedObject = -> Body [Pocket004.Sketch010.Edge2]
  _Parent = -> Elements
FEATURE [Part::FeaturePython] Element005  label="slide_axis"  # link proxy (typed FeaturePython)
  Detach = false
  LinkTransform = true
  LinkedObject = -> Body [DatumLine.]
  _Parent = -> Elements
FEATURE [Part::FeaturePython] Element006  label="slide_axis"  # link proxy (typed FeaturePython)
  Detach = false
  LinkTransform = true
  LinkedObject = -> Body002 [DatumLine001.]
  _Parent = -> Elements002
---- part ../parts/lift/upper-stage-actuator-rod.FCStd = doc fcstd_5bcfb36d5c3f ----
FCSTD DOCUMENT  (FreeCAD 0.19R18028 (Git))
Label: upper-stage-actuator-rod
License: Public Domain
LicenseURL: http://en.wikipedia.org/wiki/Public_domain
objects: Part::FeaturePython×6, App::FeaturePython×2, Sketcher::SketchObject×1, PartDesign::Pad×1, PartDesign::Body×1
note: 9 computed .brp shape members not serialized (recipe doc carries the construction recipe); baked Part::Feature solids carry a one-line shape summary decoded from their .brp

FEATURE [Sketcher::SketchObject] Sketch
  MapMode = 5
  Placement = pos=(0,0,0) rot=(0.57735,0.57735,0.57735;2.0944rad)
  Support = -> [YZ_Plane]
  sketch-geometry (1):
    g0: Circle CenterX=0 CenterY=0 CenterZ=0 NormalX=0 NormalY=0 NormalZ=1 AngleXU=0 Radius=3
  constraints (2):
    c: Coincident(g0,g-1)
    c: Radius(g0) = 3
FEATURE [PartDesign::Pad] Pad
  ClaimChildren = false
  Length = 300
  Length2 = 100
  Midplane = true
  Placement = pos=(0,0,0) rot=(0.57735,0.57735,0.57735;2.0944rad)
  Profile = -> Sketch
  Type = 0
FEATURE [PartDesign::Body] Body
  Group = -> [Sketch,Pad]
  Origin = -> Origin
  Tip = -> Pad
FEATURE [App::FeaturePython] Constraints  # WARN: FeaturePython — macro-defined, semantics opaque (R4)
  GroupMode = 1
  _Version = 1
FEATURE [Part::FeaturePython] Parts  # WARN: FeaturePython — macro-defined, semantics opaque (R4)
  Group = -> [Body]
  GroupMode = 0
FEATURE [Part::FeaturePython] Assembly  label="upper-stage-actuator-rod"  # WARN: FeaturePython — macro-defined, semantics opaque (R4)
  AutoRelax = true
  BuildShape = 0
  Freeze = false
  Group = -> [Constraints,Elements,Parts]
  GroupMode = 1
  SolverType = 1
  Verbose = false
  _SolverType = 1
  _Version = 1
FEATURE [App::FeaturePython] Elements  # WARN: FeaturePython — macro-defined, semantics opaque (R4)
  Group = -> [Element,Element001,Element002,Element003]
  GroupMode = 1
FEATURE [Part::FeaturePython] Element  label="middle"  # link proxy (typed FeaturePython)
  Detach = false
  LinkTransform = true
  LinkedObject = -> Body [Pad.Sketch.Edge1]
  _Parent = -> Elements
FEATURE [Part::FeaturePython] Element001  label="left"  # link proxy (typed FeaturePython)
  Detach = false
  LinkTransform = true
  LinkedObject = -> Body [Pad.Edge2]
  _Parent = -> Elements
FEATURE [Part::FeaturePython] Element002  label="right"  # link proxy (typed FeaturePython)
  Detach = false
  LinkTransform = true
  LinkedObject = -> Body [Pad.Edge3]
  _Parent = -> Elements
FEATURE [Part::FeaturePython] Element003  # link proxy (typed FeaturePython)
  Detach = false
  LinkTransform = true
  LinkedObject = -> Body [Pad.Edge1]
  _Parent = -> Elements
---- part ../parts/lift/upper-stage-beam.FCStd = doc fcstd_f5f9aeaa78f4 ----
FCSTD DOCUMENT  (FreeCAD 0.19R18028 (Git))
Label: upper-stage-beam
License: Public Domain
LicenseURL: http://en.wikipedia.org/wiki/Public_domain
objects: Part::FeaturePython×17, App::FeaturePython×4, Sketcher::SketchObject×3, PartDesign::Pocket×2, PartDesign::Pad×1, PartDesign::Body×1, Part::Mirroring×1
note: 26 computed .brp shape members not serialized (recipe doc carries the construction recipe); baked Part::Feature solids carry a one-line shape summary decoded from their .brp

FEATURE [Sketcher::SketchObject] Sketch
  MapMode = 5
  Support = -> [XY_Plane]
  sketch-geometry (4):
    g0: LineSegment StartX=-22 StartY=-47 StartZ=0 EndX=22 EndY=-47 EndZ=0
    g1: LineSegment StartX=22 StartY=-47 StartZ=0 EndX=22 EndY=47 EndZ=0
    g2: LineSegment StartX=22 StartY=47 StartZ=0 EndX=-22 EndY=47 EndZ=0
    g3: LineSegment StartX=-22 StartY=47 StartZ=0 EndX=-22 EndY=-47 EndZ=0
  constraints (10):
    c: Coincident(g0,g1)
    c: Coincident(g1,g2)
    c: Coincident(g2,g3)
    c: Horizontal(g2)
    c: Vertical(g3)
    c: Distance(g0) = 44
    c: Distance(g1) = 94
    c: Symmetric(g0,g0,g-2)
    c: Coincident(g3,g0)
    c: Symmetric(g0,g1,g-1)
FEATURE [PartDesign::Pad] Pad
  ClaimChildren = false
  Length = 450
  Length2 = 100
  Profile = -> Sketch
  Type = 0
FEATURE [Sketcher::SketchObject] Sketch001
  ExternalGeometry = -> [Pad]
  MapMode = 5
  Placement = pos=(22,0,0) rot=(0.57735,0.57735,0.57735;2.0944rad)
  Support = -> [Pad]
  expr: Constraints[6] = 15 + 18.5 / 2
  sketch-geometry (3):
    g0: Circle CenterX=-27 CenterY=350 CenterZ=0 NormalX=0 NormalY=0 NormalZ=1 AngleXU=0 Radius=9.25
    g1: Circle CenterX=-27 CenterY=220 CenterZ=0 NormalX=0 NormalY=0 NormalZ=1 AngleXU=0 Radius=9.25
    g2: Circle CenterX=-2.75 CenterY=430 CenterZ=0 NormalX=0 NormalY=0 NormalZ=1 AngleXU=0 Radius=3
  constraints (9):
    c: Equal(g1,g0)
    c: Diameter(g0) = 18.5
    c: Vertical(g0,g1)
    c: DistanceY(g1,g0) = 130
    c: DistanceX(g-3,g0) = 20
    c: DistanceY(g0,g-3) = 100
    c: DistanceX(g0,g2) = 24.25
    c: DistanceY(g2,g-3) = 20
    c: Diameter(g2) = 6
FEATURE [PartDesign::Pocket] Pocket
  BaseFeature = -> Pad
  ClaimChildren = false
  Length = 5
  Length2 = 100
  Profile = -> Sketch001
  Type = 1
FEATURE [Sketcher::SketchObject] Sketch002
  ExternalGeometry = -> [Pocket]
  MapMode = 5
  Placement = pos=(22,0,0) rot=(0.57735,0.57735,0.57735;2.0944rad)
  Support = -> [Pocket]
  expr: Constraints[3] = 45 / 2
  sketch-geometry (3):
    g0: Circle CenterX=24.5 CenterY=425 CenterZ=0 NormalX=0 NormalY=0 NormalZ=1 AngleXU=0 Radius=1.5
    g1: Circle CenterX=24.5 CenterY=265 CenterZ=0 NormalX=0 NormalY=0 NormalZ=1 AngleXU=0 Radius=1.5
    g2: Circle CenterX=24.5 CenterY=73 CenterZ=0 NormalX=0 NormalY=0 NormalZ=1 AngleXU=0 Radius=1.5
  constraints (9):
    c: Equal(g2,g1)
    c: Equal(g1,g0)
    c: Diameter(g0) = 3
    c: DistanceX(g0,g-3) = 22.5
    c: DistanceY(g0,g-3) = 25
    c: Vertical(g0,g1)
    c: Vertical(g1,g2)
    c: DistanceY(g1,g0) = 160
    c: DistanceY(g2,g0) = 352
FEATURE [PartDesign::Pocket] Pocket001
  BaseFeature = -> Pocket
  ClaimChildren = false
  Length = 10
  Length2 = 100
  Profile = -> Sketch002
  Type = 0
FEATURE [PartDesign::Body] Body
  Group = -> [Sketch,Pad,Sketch001,Pocket,Sketch002,Pocket001]
  Origin = -> Origin
  SingleSolid = true
  Tip = -> Pocket001
FEATURE [Part::Mirroring] Part__Mirroring  label="Pocket001 (Mirror #1)"
  Base = (0,0,0)
  Normal = (1,0,0)
  Placement = pos=(246,0,0) rot=(0,0,1;0rad)
  Source = -> Pocket001
FEATURE [App::FeaturePython] Constraints  # WARN: FeaturePython — macro-defined, semantics opaque (R4)
  GroupMode = 1
  _Version = 1
FEATURE [Part::FeaturePython] Parts  # WARN: FeaturePython — macro-defined, semantics opaque (R4)
  Group = -> [Body]
  GroupMode = 0
FEATURE [App::FeaturePython] Constraints001  # WARN: FeaturePython — macro-defined, semantics opaque (R4)
  GroupMode = 1
  _Version = 1
FEATURE [Part::FeaturePython] Parts001  # WARN: FeaturePython — macro-defined, semantics opaque (R4)
  Group = -> [Part__Mirroring]
  GroupMode = 0
FEATURE [Part::FeaturePython] Assembly  label="upper-stage-beam-left"  # WARN: FeaturePython — macro-defined, semantics opaque (R4)
  AutoRelax = true
  BuildShape = 0
  Freeze = false
  Group = -> [Constraints,Elements,Parts]
  GroupMode = 1
  SolverType = 1
  Verbose = false
  _SolverType = 1
  _Version = 1
FEATURE [App::FeaturePython] Elements  # WARN: FeaturePython — macro-defined, semantics opaque (R4)
  Group = -> [Element,Element001,Element003,Element004,Element005,Element006,Element013]
  GroupMode = 1
FEATURE [Part::FeaturePython] Assembly001  label="upper-stage-beam-right"  # WARN: FeaturePython — macro-defined, semantics opaque (R4)
  AutoRelax = true
  BuildShape = 0
  Freeze = false
  Group = -> [Constraints001,Elements001,Parts001]
  GroupMode = 1
  SolverType = 1
  Verbose = false
  _SolverType = 1
  _Version = 1
FEATURE [App::FeaturePython] Elements001  # WARN: FeaturePython — macro-defined, semantics opaque (R4)
  Group = -> [Element007,Element008,Element009,Element010,Element011,Element012]
  GroupMode = 1
FEATURE [Part::FeaturePython] Element  label="tv_rod_hole_top"  # link proxy (typed FeaturePython)
  Detach = false
  LinkTransform = true
  LinkedObject = -> Body [Pocket.Sketch001.Edge1]
  _Parent = -> Elements
FEATURE [Part::FeaturePython] Element001  label="tv_rod_hole_bottom"  # link proxy (typed FeaturePython)
  Detach = false
  LinkTransform = true
  LinkedObject = -> Body [Pocket.Sketch001.Edge2]
  _Parent = -> Elements
FEATURE [Part::FeaturePython] Element003  label="rail_hole_top"  # link proxy (typed FeaturePython)
  Detach = false
  LinkTransform = true
  LinkedObject = -> Body [Pocket001.Sketch002.Edge1]
  _Parent = -> Elements
FEATURE [Part::FeaturePython] Element004  label="rail-hole-middle"  # link proxy (typed FeaturePython)
  Detach = false
  LinkTransform = true
  LinkedObject = -> Body [Pocket001.Sketch002.Edge2]
  _Parent = -> Elements
FEATURE [Part::FeaturePython] Element005  label="rail_hole_bottom"  # link proxy (typed FeaturePython)
  Detach = false
  LinkTransform = true
  LinkedObject = -> Body [Pocket001.Sketch002.Edge3]
  _Parent = -> Elements
FEATURE [Part::FeaturePython] Element006  label="actuator_rod_hole"  # link proxy (typed FeaturePython)
  Detach = false
  LinkTransform = true
  LinkedObject = -> Body [Pocket.Sketch001.Edge3]
  _Parent = -> Elements
FEATURE [Part::FeaturePython] Element007  label="tv_rod_hole_top"  # link proxy (typed FeaturePython)
  Detach = false
  LinkTransform = true
  LinkedObject = -> Part__Mirroring [Edge18]
  _Parent = -> Elements001
FEATURE [Part::FeaturePython] Element008  label="tv_rod_hole_bottom"  # link proxy (typed FeaturePython)
  Detach = false
  LinkTransform = true
  LinkedObject = -> Part__Mirroring [Edge14]
  _Parent = -> Elements001
FEATURE [Part::FeaturePython] Element009  label="actuator_rod_hole"  # link proxy (typed FeaturePython)
  Detach = false
  LinkTransform = true
  LinkedObject = -> Part__Mirroring [Edge19]
  _Parent = -> Elements001
FEATURE [Part::FeaturePython] Element010  label="rail_hole_top"  # link proxy (typed FeaturePython)
  Detach = false
  LinkTransform = true
  LinkedObject = -> Part__Mirroring [Edge16]
  _Parent = -> Elements001
FEATURE [Part::FeaturePython] Element011  label="rail_hole_middle"  # link proxy (typed FeaturePython)
  Detach = false
  LinkTransform = true
  LinkedObject = -> Part__Mirroring [Edge17]
  _Parent = -> Elements001
FEATURE [Part::FeaturePython] Element012  label="rail_hole_bottom"  # link proxy (typed FeaturePython)
  Detach = false
  LinkTransform = true
  LinkedObject = -> Part__Mirroring [Edge15]
  _Parent = -> Elements001
FEATURE [Part::FeaturePython] Element013  label="base_edge"  # link proxy (typed FeaturePython)
  Detach = false
  LinkTransform = true
  LinkedObject = -> Body [Pad.Sketch.Edge4]
  _Parent = -> Elements
---- part ../parts/lift/upper-stage-rod.FCStd = doc fcstd_2fb69f4102b5 ----
FCSTD DOCUMENT  (FreeCAD 0.19R18028 (Git))
Label: upper-stage-rod
License: Public Domain
LicenseURL: http://en.wikipedia.org/wiki/Public_domain
objects: Part::FeaturePython×5, App::FeaturePython×2, Sketcher::SketchObject×1, PartDesign::Pad×1, PartDesign::Body×1
note: 8 computed .brp shape members not serialized (recipe doc carries the construction recipe); baked Part::Feature solids carry a one-line shape summary decoded from their .brp

FEATURE [App::FeaturePython] Constraints  # WARN: FeaturePython — macro-defined, semantics opaque (R4)
  GroupMode = 1
  _Version = 1
FEATURE [Sketcher::SketchObject] Sketch
  MapMode = 5
  Placement = pos=(0,0,0) rot=(0.57735,0.57735,0.57735;2.0944rad)
  Support = -> [YZ_Plane]
  sketch-geometry (1):
    g0: Circle CenterX=0 CenterY=0 CenterZ=0 NormalX=0 NormalY=0 NormalZ=1 AngleXU=0 Radius=9
  constraints (2):
    c: Coincident(g0,g-1)
    c: Radius(g0) = 9
FEATURE [PartDesign::Pad] Pad
  ClaimChildren = false
  Length = 450
  Length2 = 100
  Midplane = true
  Placement = pos=(0,0,0) rot=(0.57735,0.57735,0.57735;2.0944rad)
  Profile = -> Sketch
  Type = 0
FEATURE [PartDesign::Body] Body
  Group = -> [Sketch,Pad]
  Origin = -> Origin
  Tip = -> Pad
FEATURE [Part::FeaturePython] Parts  # WARN: FeaturePython — macro-defined, semantics opaque (R4)
  Group = -> [Body]
  GroupMode = 0
FEATURE [Part::FeaturePython] Assembly  label="upper-stage-rod"  # WARN: FeaturePython — macro-defined, semantics opaque (R4)
  AutoRelax = true
  BuildShape = 0
  Freeze = false
  Group = -> [Constraints,Elements,Parts]
  GroupMode = 1
  SolverType = 1
  Verbose = false
  _SolverType = 1
  _Version = 1
FEATURE [App::FeaturePython] Elements  # WARN: FeaturePython — macro-defined, semantics opaque (R4)
  Group = -> [Element,Element001,Element002]
  GroupMode = 1
FEATURE [Part::FeaturePython] Element  label="middle"  # link proxy (typed FeaturePython)
  Detach = false
  LinkTransform = true
  LinkedObject = -> Body [Pad.Sketch.Edge1]
  _Parent = -> Elements
FEATURE [Part::FeaturePython] Element001  label="left"  # link proxy (typed FeaturePython)
  Detach = false
  LinkTransform = true
  LinkedObject = -> Body [Pad.Edge2]
  _Parent = -> Elements
FEATURE [Part::FeaturePython] Element002  label="right"  # link proxy (typed FeaturePython)
  Detach = false
  LinkTransform = true
  LinkedObject = -> Body [Pad.Edge3]
  _Parent = -> Elements
